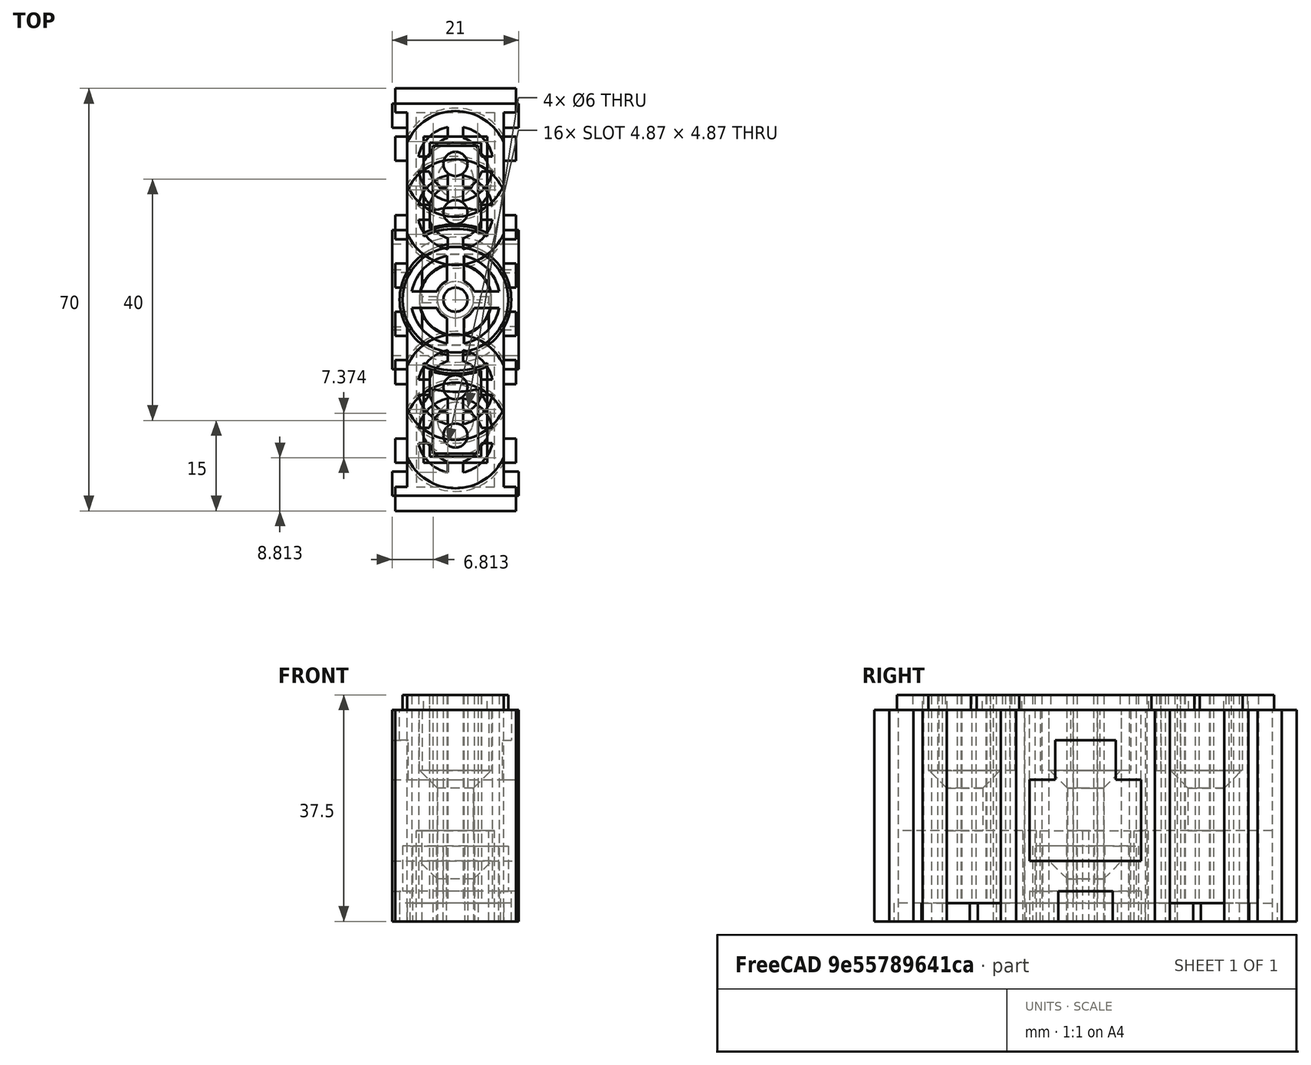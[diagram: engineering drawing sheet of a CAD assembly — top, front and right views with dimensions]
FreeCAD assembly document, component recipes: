
FREECAD ASSEMBLY — COMPONENT RECIPES ("PipeMountDistance")

This assembly document has 5 components, labeled P0..P4 below (a component is one placed body or linked part). 5 of them carry a construction recipe — the FreeCAD feature program that regenerates the part from scratch, quoted from this document or its linked companion documents; the rest are supplied as boundary geometry only. No exploded tour is included for this assembly.
COMPONENT P0 — recipe-attached ("Dual Pipes 40mm", modeled in this document).
Construction recipe (the document's own serialized feature program — sketch geometry with constraints, then the solid features built on it; lengths are millimeters unless a unit is written):

FEATURE [Sketcher::SketchObject] Sketch
  ArcFitTolerance = 1e-06
  AttachmentSupport = -> [XY_Plane]
  ExternalTypes = [0]
  FullyConstrained = true
  MakeInternals = false
  MapMode = 5
  sketch-geometry (23):
    g0: LineSegment StartX=-10.5 StartY=-11.5 StartZ=0 EndX=-10.5 EndY=11.5 EndZ=0
    g1: LineSegment StartX=-10.5 StartY=11.5 StartZ=0 EndX=-8 EndY=11.5 EndZ=0
    g2: LineSegment StartX=-8 StartY=11.5 StartZ=0 EndX=-8 EndY=28.5 EndZ=0
    g3: LineSegment StartX=-8 StartY=28.5 StartZ=0 EndX=-10.5 EndY=28.5 EndZ=0
    g4: LineSegment StartX=-10.5 StartY=28.5 StartZ=0 EndX=-10.5 EndY=32.5 EndZ=0
    g5: LineSegment StartX=-10.5 StartY=32.5 StartZ=0 EndX=10.5 EndY=32.5 EndZ=0
    g6: LineSegment StartX=10.5 StartY=32.5 StartZ=0 EndX=10.5 EndY=28.5 EndZ=0
    g7: LineSegment StartX=10.5 StartY=28.5 StartZ=0 EndX=8 EndY=28.5 EndZ=0
    g8: LineSegment StartX=8 StartY=28.5 StartZ=0 EndX=8 EndY=11.5 EndZ=0
    g9: LineSegment StartX=8 StartY=11.5 StartZ=0 EndX=10.5 EndY=11.5 EndZ=0
    g10: LineSegment StartX=10.5 StartY=11.5 StartZ=0 EndX=10.5 EndY=-11.5 EndZ=0
    g11: LineSegment StartX=10.5 StartY=-11.5 StartZ=0 EndX=8 EndY=-11.5 EndZ=0
    g12: LineSegment StartX=8 StartY=-11.5 StartZ=0 EndX=8 EndY=-28.5 EndZ=0
    g13: LineSegment StartX=8 StartY=-28.5 StartZ=0 EndX=10.5 EndY=-28.5 EndZ=0
    g14: LineSegment StartX=10.5 StartY=-28.5 StartZ=0 EndX=10.5 EndY=-32.5 EndZ=0
    g15: LineSegment StartX=10.5 StartY=-32.5 StartZ=0 EndX=-10.5 EndY=-32.5 EndZ=0
    g16: LineSegment StartX=-10.5 StartY=-32.5 StartZ=0 EndX=-10.5 EndY=-28.5 EndZ=0
    g17: LineSegment StartX=-10.5 StartY=-28.5 StartZ=0 EndX=-8 EndY=-28.5 EndZ=0
    g18: LineSegment StartX=-8 StartY=-28.5 StartZ=0 EndX=-8 EndY=-11.5 EndZ=0
    g19: LineSegment StartX=-8 StartY=-11.5 StartZ=0 EndX=-10.5 EndY=-11.5 EndZ=0
    g20: Circle CenterX=0 CenterY=0 CenterZ=0 NormalX=0 NormalY=0 NormalZ=1 AngleXU=0 Radius=2
    g21: Circle CenterX=0 CenterY=20 CenterZ=0 NormalX=0 NormalY=0 NormalZ=1 AngleXU=0 Radius=3
    g22: Circle CenterX=0 CenterY=-20 CenterZ=0 NormalX=0 NormalY=0 NormalZ=1 AngleXU=0 Radius=3
  constraints (65):
    c: Vertical(g0)
    c: Coincident(g0,g1)
    c: Coincident(g1,g2)
    c: Coincident(g2,g3)
    c: Coincident(g3,g4)
    c: Coincident(g4,g5)
    c: Coincident(g5,g6)
    c: Coincident(g6,g7)
    c: Coincident(g7,g8)
    c: Coincident(g8,g9)
    c: Horizontal(g9)
    c: Coincident(g9,g10)
    c: Coincident(g10,g11)
    c: Coincident(g11,g12)
    c: Vertical(g12)
    c: Coincident(g12,g13)
    c: Horizontal(g13)
    c: Coincident(g13,g14)
    c: Coincident(g14,g15)
    c: Horizontal(g15)
    c: Coincident(g15,g16)
    c: Coincident(g16,g17)
    c: Horizontal(g17)
    c: Coincident(g17,g18)
    c: Coincident(g18,g19)
    c: Coincident(g19,g0)
    c: Horizontal(g3)
    c: Horizontal(g1)
    c: Horizontal(g19)
    c: Horizontal(g11)
    c: Horizontal(g7)
    c: Vertical(g6)
    c: Vertical(g2)
    c: Vertical(g8)
    c: Vertical(g18)
    c: Vertical(g16)
    c: Vertical(g14)
    c: Symmetric(g4,g5,g-2)
    c: Symmetric(g9,g10,g-1)
    c: Equal(g5,g15)
    c: Equal(g7,g9)
    c: DistanceX(g2,g7) = 16  'MinorWidth'
    c: DistanceX(g5,g5) = 21  'MajorWidth'
    c: DistanceY(g15,g4) = 65  'MinorHeight'
    c: DistanceY(g2,g2) = 17  'CutoutHeight'
    c: Diameter(g20) = 4  'ScrewHoleDia'
    c: PointOnObject(g21,g-2)
    c: Symmetric(g22,g21,g-1)
    c: DistanceY(g22,g21) = 40
    c: Equal(g21,g22)
    c: Diameter(g22) = 6  'MountHoleDia'
    c: Coincident(g20,g-1)
    c: Vertical(g4)
    c: Equal(g6,g4)
    c: Equal(g4,g16)
    c: Equal(g16,g14)
    c: Symmetric(g4,g15,g-1)
    c: Equal(g3,g19)
    c: Equal(g19,g11)
    c: Equal(g11,g7)
    c: Equal(g10,g0)
    c: Equal(g2,g8)
    c: DistanceY(g0,g0) = 23
    c: Vertical(g1,g18)
    c: DistanceY(g6,g6) = 4
FEATURE [PartDesign::Pad] Pad
  Direction = (0,0,1)
  Length = 35
  Length2 = 10
  Profile = -> Sketch
  ReferenceAxis = -> Sketch [N_Axis]
  Refine = true
  Suppressed = false
  Type = 0
FEATURE [Sketcher::SketchObject] Sketch001
  ArcFitTolerance = 1e-06
  AttachmentSupport = -> [Pad]
  ExternalTypes = [0]
  FullyConstrained = true
  MakeInternals = false
  MapMode = 5
  Placement = pos=(0,0,0) rot=(1,0,0;3.14159rad)
  sketch-geometry (1):
    g0: Circle CenterX=0 CenterY=0 CenterZ=0 NormalX=0 NormalY=0 NormalZ=1 AngleXU=0 Radius=9.25
  constraints (2):
    c: Diameter(g0) = 18.5  'PadDia'
    c: Coincident(g0,g-1)
FEATURE [PartDesign::Pocket] Pocket
  BaseFeature = -> Pad
  Direction = (0,0,1)
  Length = 3
  Length2 = 5
  Profile = -> Sketch001
  ReferenceAxis = -> Sketch001 [N_Axis]
  Refine = true
  Suppressed = false
  Type = 0
FEATURE [Sketcher::SketchObject] Sketch002
  ArcFitTolerance = 1e-06
  AttachmentSupport = -> [Pocket]
  ExternalGeometry = -> [Pocket]
  ExternalTypes = [0]
  FullyConstrained = true
  MakeInternals = false
  MapMode = 5
  Placement = pos=(0,0,35) rot=(0,0,1;0rad)
  expr: .Constraints.MinorPadDia = <<Sketch001>>.Constraints.PadDia - 1 mm
  expr: .Constraints.WidePadDia = .Constraints.MinorPadDia + 6 mm
  sketch-geometry (12):
    g0: Circle CenterX=0 CenterY=0 CenterZ=0 NormalX=0 NormalY=0 NormalZ=1 AngleXU=0 Radius=8.75
    g1: Circle CenterX=0 CenterY=0 CenterZ=0 NormalX=0 NormalY=0 NormalZ=1 AngleXU=0 Radius=2
    g2: Circle CenterX=0 CenterY=20 CenterZ=0 NormalX=0 NormalY=0 NormalZ=1 AngleXU=0 Radius=3
    g3: Circle CenterX=0 CenterY=-20 CenterZ=0 NormalX=0 NormalY=0 NormalZ=1 AngleXU=0 Radius=3
    g4: LineSegment StartX=-5.25 StartY=10.5119 StartZ=0 EndX=-5.25 EndY=27 EndZ=0
    g5: LineSegment StartX=-5.25 StartY=27 StartZ=0 EndX=5.25 EndY=27 EndZ=0
    g6: LineSegment StartX=5.25 StartY=27 StartZ=0 EndX=5.25 EndY=10.5119 EndZ=0
    g7: LineSegment StartX=-5.25 StartY=-10.5119 StartZ=0 EndX=-5.25 EndY=-27 EndZ=0
    g8: LineSegment StartX=-5.25 StartY=-27 StartZ=0 EndX=5.25 EndY=-27 EndZ=0
    g9: LineSegment StartX=5.25 StartY=-27 StartZ=0 EndX=5.25 EndY=-10.5119 EndZ=0
    g10: ArcOfCircle CenterX=0 CenterY=0 CenterZ=0 NormalX=0 NormalY=0 NormalZ=1 AngleXU=0 Radius=11.75 StartAngle=1.1076 EndAngle=2.03399
    g11: ArcOfCircle CenterX=0 CenterY=0 CenterZ=0 NormalX=0 NormalY=0 NormalZ=1 AngleXU=0 Radius=11.75 StartAngle=4.24919 EndAngle=5.17558
  constraints (33):
    c: Coincident(g0,g-1)
    c: Coincident(g1,g0)
    c: Equal(g-3,g1)
    c: Diameter(g0) = 17.5  'MinorPadDia'
    c: Coincident(g2,g-4)
    c: Symmetric(g3,g2,g-1)
    c: Equal(g2,g3)
    c: Equal(g2,g-4)
    c: Vertical(g4)
    c: Coincident(g4,g5)
    c: Horizontal(g5)
    c: Coincident(g5,g6)
    c: Vertical(g6)
    c: Vertical(g7)
    c: Coincident(g7,g8)
    c: Horizontal(g8)
    c: Coincident(g8,g9)
    c: Vertical(g9)
    c: Equal(g5,g8)
    c: Equal(g9,g7)
    c: Equal(g7,g4)
    c: Equal(g4,g6)
    c: Coincident(g10,g4)
    c: Coincident(g10,g6)
    c: Coincident(g11,g7)
    c: Coincident(g11,g9)
    c: Coincident(g11,g10)
    c: Coincident(g11,g0)
    c: Equal(g10,g11)
    c: Diameter(g10) = 23.5  'WidePadDia'
    c: DistanceX(g5,g-6) = 2.75  'OuterWallWidth'
    c: DistanceX(g5,g5) = 10.5
    c: DistanceY(g7,g4) = 54
FEATURE [PartDesign::Pad] Pad001
  BaseFeature = -> Pocket
  Direction = (0,0,1)
  Length = 2.5
  Length2 = 10
  Profile = -> Sketch002
  ReferenceAxis = -> Sketch002 [N_Axis]
  Refine = true
  Suppressed = false
  Type = 0
FEATURE [Sketcher::SketchObject] Sketch003
  ArcFitTolerance = 1e-06
  AttachmentSupport = -> [Pad001]
  ExternalGeometry = -> [Pad001]
  ExternalTypes = [0]
  FullyConstrained = true
  MakeInternals = false
  MapMode = 5
  Placement = pos=(0,0,37.5) rot=(0,0,1;0rad)
  expr: Constraints[22] = .Constraints.InnerWallWidth
  expr: Constraints[23] = Sketch002.Constraints.WidePadDia + .Constraints.InnerWallWidth * 1.5
  sketch-geometry (8):
    g0: LineSegment StartX=-4.25 StartY=11.7553 StartZ=0 EndX=-4.25 EndY=26 EndZ=0
    g1: LineSegment StartX=-4.25 StartY=26 StartZ=0 EndX=4.25 EndY=26 EndZ=0
    g2: LineSegment StartX=4.25 StartY=26 StartZ=0 EndX=4.25 EndY=11.7553 EndZ=0
    g3: LineSegment StartX=-4.25 StartY=-11.7553 StartZ=0 EndX=-4.25 EndY=-26 EndZ=0
    g4: LineSegment StartX=-4.25 StartY=-26 StartZ=0 EndX=4.25 EndY=-26 EndZ=0
    g5: LineSegment StartX=4.25 StartY=-26 StartZ=0 EndX=4.25 EndY=-11.7553 EndZ=0
    g6: ArcOfCircle CenterX=0 CenterY=0 CenterZ=0 NormalX=0 NormalY=0 NormalZ=1 AngleXU=0 Radius=12.5 StartAngle=4.36547 EndAngle=5.05931
    g7: ArcOfCircle CenterX=0 CenterY=0 CenterZ=0 NormalX=0 NormalY=0 NormalZ=1 AngleXU=0 Radius=12.5 StartAngle=1.22388 EndAngle=1.91771
  constraints (26):
    c: Vertical(g0)
    c: Coincident(g0,g1)
    c: Horizontal(g1)
    c: Coincident(g1,g2)
    c: Vertical(g2)
    c: Vertical(g3)
    c: Coincident(g3,g4)
    c: Horizontal(g4)
    c: Coincident(g4,g5)
    c: Vertical(g5)
    c: Coincident(g6,g3)
    c: Coincident(g6,g5)
    c: Coincident(g7,g0)
    c: Coincident(g7,g2)
    c: Coincident(g6,g-1)
    c: Coincident(g6,g7)
    c: Equal(g2,g0)
    c: Equal(g0,g3)
    c: Equal(g3,g5)
    c: Equal(g6,g7)
    c: Equal(g4,g1)
    c: DistanceX(g1,g-4) = 1  'InnerWallWidth'
    c: DistanceY(g1,g-4) = 1
    c: Diameter(g7) = 25
    c: Diameter(g-5) = 17.5  'D2'
    c: Diameter(g-6) = 23.5  'D3'
FEATURE [PartDesign::Pocket] Pocket001
  BaseFeature = -> Pad001
  Direction = (0,0,-1)
  Length = 0
  Length2 = 5
  Offset = 25
  Profile = -> Sketch003
  ReferenceAxis = -> Sketch003 [N_Axis]
  Refine = true
  Suppressed = false
  Type = 3
  UpToFace = -> Pad001 [Face4]
FEATURE [Sketcher::SketchObject] Sketch004
  ArcFitTolerance = 1e-06
  AttachmentSupport = -> [Pocket001]
  ExternalGeometry = -> [Pocket001]
  ExternalTypes = [0]
  FullyConstrained = true
  MakeInternals = false
  MapMode = 5
  Placement = pos=(0,0,37.5) rot=(0,0,1;0rad)
  expr: Constraints[44] = <<Sketch002>>.Constraints.OuterWallWidth
  expr: Constraints[45] = <<Sketch002>>.Constraints.OuterWallWidth
  expr: Constraints[48] = <<Sketch002>>.Constraints.MinorPadDia - <<Sketch002>>.Constraints.OuterWallWidth
  expr: Constraints[49] = <<Sketch>>.Constraints.ScrewHoleDia + <<Sketch002>>.Constraints.OuterWallWidth
  sketch-geometry (16):
    g0: ArcOfCircle CenterX=0 CenterY=0 CenterZ=0 NormalX=0 NormalY=0 NormalZ=1 AngleXU=0 Radius=7.375 StartAngle=1.75833 EndAngle=2.95405
    g1: ArcOfCircle CenterX=0 CenterY=0 CenterZ=0 NormalX=0 NormalY=0 NormalZ=1 AngleXU=0 Radius=3.375 StartAngle=1.99041 EndAngle=2.72198
    g2: ArcOfCircle CenterX=-3e-16 CenterY=9e-16 CenterZ=0 NormalX=0 NormalY=0 NormalZ=1 AngleXU=0 Radius=7.375 StartAngle=0.187538 EndAngle=1.38326
    g3: ArcOfCircle CenterX=0 CenterY=0 CenterZ=0 NormalX=0 NormalY=0 NormalZ=1 AngleXU=0 Radius=3.375 StartAngle=0.419613 EndAngle=1.15118
    g4: ArcOfCircle CenterX=0 CenterY=0 CenterZ=0 NormalX=0 NormalY=0 NormalZ=1 AngleXU=0 Radius=3.375 StartAngle=5.132 EndAngle=5.86357
    g5: ArcOfCircle CenterX=0 CenterY=0 CenterZ=0 NormalX=0 NormalY=0 NormalZ=1 AngleXU=0 Radius=7.375 StartAngle=4.89993 EndAngle=6.09565
    g6: ArcOfCircle CenterX=0 CenterY=0 CenterZ=0 NormalX=0 NormalY=0 NormalZ=1 AngleXU=0 Radius=3.375 StartAngle=3.56121 EndAngle=4.29278
    g7: ArcOfCircle CenterX=-8e-16 CenterY=2e-16 CenterZ=0 NormalX=0 NormalY=0 NormalZ=1 AngleXU=0 Radius=7.375 StartAngle=3.32913 EndAngle=4.52485
    g8: LineSegment StartX=3.08221 StartY=1.375 StartZ=0 EndX=7.24569 EndY=1.375 EndZ=0
    g9: LineSegment StartX=3.08221 StartY=-1.375 StartZ=0 EndX=7.24569 EndY=-1.375 EndZ=0
    g10: LineSegment StartX=-1.375 StartY=3.08221 StartZ=0 EndX=-1.375 EndY=7.24569 EndZ=0
    g11: LineSegment StartX=1.375 StartY=3.08221 StartZ=0 EndX=1.375 EndY=7.24569 EndZ=0
    g12: LineSegment StartX=-3.08221 StartY=1.375 StartZ=0 EndX=-7.24569 EndY=1.375 EndZ=0
    g13: LineSegment StartX=-7.24569 StartY=-1.375 StartZ=0 EndX=-3.08221 EndY=-1.375 EndZ=0
    g14: LineSegment StartX=1.375 StartY=-7.24569 StartZ=0 EndX=1.375 EndY=-3.08221 EndZ=0
    g15: LineSegment StartX=-1.375 StartY=-7.24569 StartZ=0 EndX=-1.375 EndY=-3.08221 EndZ=0
  constraints (52):
    c: Coincident(g4,g5)
    c: Coincident(g4,g6)
    c: Coincident(g4,g0)
    c: Coincident(g4,g1)
    c: Coincident(g4,g3)
    c: Coincident(g4,g-1)
    c: Equal(g3,g4)
    c: Equal(g4,g6)
    c: Equal(g6,g1)
    c: Equal(g0,g2)
    c: Equal(g2,g5)
    c: Equal(g5,g7)
    c: Coincident(g8,g3)
    c: Coincident(g8,g2)
    c: Horizontal(g8)
    c: Coincident(g9,g4)
    c: Coincident(g9,g5)
    c: Horizontal(g9)
    c: Coincident(g10,g1)
    c: Coincident(g10,g0)
    c: Coincident(g11,g3)
    c: Coincident(g11,g2)
    c: Coincident(g12,g1)
    c: Coincident(g12,g0)
    c: Coincident(g13,g7)
    c: Coincident(g13,g6)
    c: Horizontal(g13)
    c: Coincident(g14,g5)
    c: Coincident(g14,g4)
    c: Coincident(g15,g7)
    c: Coincident(g15,g6)
    c: Vertical(g15)
    c: Vertical(g14)
    c: Vertical(g11)
    c: Vertical(g10)
    c: Horizontal(g12)
    c: Vertical(g5,g2)
    c: Vertical(g4,g3)
    c: Vertical(g6,g1)
    c: Vertical(g7,g0)
    c: Horizontal(g0,g2)
    c: Horizontal(g1,g3)
    c: Horizontal(g6,g4)
    c: Horizontal(g7,g5)
    c: DistanceY(g5,g2) = 2.75
    c: DistanceX(g0,g2) = 2.75
    c: Diameter(g-3) = 17.5
    c: Diameter(g-4) = 4
    c: Diameter(g2) = 14.75
    c: Diameter(g3) = 6.75
    c: Horizontal(g1,g3)
    c: Vertical(g6,g1)
FEATURE [PartDesign::Pocket] Pocket002
  BaseFeature = -> Pocket001
  Direction = (0,0,-1)
  Length = 5
  Length2 = 5
  Profile = -> Sketch004
  ReferenceAxis = -> Sketch004 [N_Axis]
  Refine = true
  Suppressed = false
  Type = 1
FEATURE [Sketcher::SketchObject] Sketch005
  ArcFitTolerance = 1e-06
  AttachmentSupport = -> [Pocket002]
  ExternalGeometry = -> [Pocket002]
  ExternalTypes = [0]
  FullyConstrained = true
  MakeInternals = false
  MapMode = 5
  Placement = pos=(0,0,37.5) rot=(0,0,1;0rad)
  sketch-geometry (2):
    g0: Circle CenterX=0 CenterY=20 CenterZ=0 NormalX=0 NormalY=0 NormalZ=1 AngleXU=0 Radius=6
    g1: Circle CenterX=0 CenterY=-20 CenterZ=0 NormalX=0 NormalY=0 NormalZ=1 AngleXU=0 Radius=6
  constraints (4):
    c: Coincident(g0,g-3)
    c: Equal(g1,g0)
    c: Symmetric(g1,g0,g-1)
    c: Diameter(g0) = 12
FEATURE [PartDesign::Pocket] Pocket003
  BaseFeature = -> Pocket002
  Direction = (0,0,-1)
  Length = 0
  Length2 = 5
  Profile = -> Sketch005
  ReferenceAxis = -> Sketch005 [N_Axis]
  Refine = true
  Suppressed = false
  Type = 3
  UpToFace = -> Pocket002 [Face35]
FEATURE [Sketcher::SketchObject] Sketch006
  ArcFitTolerance = 1e-06
  ExternalTypes = [0]
  FullyConstrained = true
  MakeInternals = false
  MapMode = 5
  Placement = pos=(0,0,0) rot=(1,0,0;3.14159rad)
  expr: Constraints[16] = .Constraints.BottomWallWidth
  expr: Constraints[23] = Sketch001.Constraints.PadDia + .Constraints.BottomWallWidth * 1.5
  sketch-geometry (8):
    g0: LineSegment StartX=-6.5 StartY=8.08645 StartZ=0 EndX=-6.5 EndY=31 EndZ=0
    g1: LineSegment StartX=-6.5 StartY=31 StartZ=0 EndX=6.5 EndY=31 EndZ=0
    g2: LineSegment StartX=6.5 StartY=31 StartZ=0 EndX=6.5 EndY=8.08645 EndZ=0
    g3: LineSegment StartX=-6.5 StartY=-8.08645 StartZ=0 EndX=-6.5 EndY=-31 EndZ=0
    g4: LineSegment StartX=-6.5 StartY=-31 StartZ=0 EndX=6.5 EndY=-31 EndZ=0
    g5: LineSegment StartX=6.5 StartY=-31 StartZ=0 EndX=6.5 EndY=-8.08645 EndZ=0
    g6: ArcOfCircle CenterX=0 CenterY=0 CenterZ=0 NormalX=0 NormalY=0 NormalZ=1 AngleXU=0 Radius=10.375 StartAngle=4.03533 EndAngle=5.38945
    g7: ArcOfCircle CenterX=0 CenterY=0 CenterZ=0 NormalX=0 NormalY=0 NormalZ=1 AngleXU=0 Radius=10.375 StartAngle=0.893734 EndAngle=2.24786
  constraints (25):
    c: Vertical(g0)
    c: Coincident(g0,g1)
    c: Horizontal(g1)
    c: Coincident(g1,g2)
    c: Vertical(g2)
    c: Vertical(g3)
    c: Coincident(g3,g4)
    c: Horizontal(g4)
    c: Coincident(g4,g5)
    c: Vertical(g5)
    c: Coincident(g6,g3)
    c: Coincident(g6,g5)
    c: Coincident(g7,g0)
    c: Coincident(g7,g2)
    c: Coincident(g7,g6)
    c: Coincident(g7,g-1)
    c: DistanceY(g1,g-3) = 1.5
    c: DistanceX(g1,g-4) = 1.5  'BottomWallWidth'
    c: Equal(g2,g0)
    c: Equal(g0,g3)
    c: Equal(g3,g5)
    c: Equal(g6,g7)
    c: Diameter(g-5) = 18
    c: Diameter(g7) = 20.75
    c: Equal(g4,g1)
FEATURE [PartDesign::Pocket] Pocket004
  BaseFeature = -> Pocket003
  Direction = (0,0,1)
  Length = 0
  Length2 = 5
  Offset = 10
  Profile = -> Sketch006
  ReferenceAxis = -> Sketch006 [N_Axis]
  Refine = true
  Suppressed = false
  Type = 3
  UpToFace = -> Pocket003 [Face75]
FEATURE [PartDesign::Chamfer] Chamfer
  Angle = 45
  Base = -> Pocket004 [Edge191,Edge222]
  BaseFeature = -> Pocket004
  ChamferType = 0
  FlipDirection = false
  Refine = true
  Size = 2.9
  Size2 = 1
  SupportTransform = false
  Suppressed = false
  UseAllEdges = false
FEATURE [PartDesign::Body] Body  label="Dual Pipes 40mm"
  AllowCompound = false
  Group = -> [Sketch,Pad,Sketch001,Pocket,Sketch002,Pad001,Sketch003,Pocket001,Sketch004,Pocket002,Sketch005,Pocket003,Sketch006,Pocket004,Chamfer]
  Origin = -> Origin
  Tip = -> Chamfer
COMPONENT P1 — recipe-attached ("Dual Pipes 45mm", modeled in this document).
Construction recipe (the document's own serialized feature program — sketch geometry with constraints, then the solid features built on it; lengths are millimeters unless a unit is written):

FEATURE [Sketcher::SketchObject] Sketch007
  ArcFitTolerance = 1e-06
  AttachmentSupport = -> [XY_Plane001]
  ExternalTypes = [0]
  FullyConstrained = true
  MakeInternals = false
  MapMode = 5
  sketch-geometry (32):
    g0: LineSegment StartX=-10 StartY=35 StartZ=0 EndX=-10 EndY=31 EndZ=0
    g1: LineSegment StartX=-10 StartY=31 StartZ=0 EndX=-8 EndY=31 EndZ=0
    g2: LineSegment StartX=-8 StartY=31 StartZ=0 EndX=-8 EndY=14 EndZ=0
    g3: LineSegment StartX=-8 StartY=14 StartZ=0 EndX=-10 EndY=14 EndZ=0
    g4: LineSegment StartX=-10 StartY=-14 StartZ=0 EndX=-8 EndY=-14 EndZ=0
    g5: LineSegment StartX=-8 StartY=-14 StartZ=0 EndX=-8 EndY=-31 EndZ=0
    g6: LineSegment StartX=-8 StartY=-31 StartZ=0 EndX=-10 EndY=-31 EndZ=0
    g7: LineSegment StartX=-10 StartY=-31 StartZ=0 EndX=-10 EndY=-35 EndZ=0
    g8: LineSegment StartX=-10 StartY=-35 StartZ=0 EndX=10 EndY=-35 EndZ=0
    g9: LineSegment StartX=10 StartY=-35 StartZ=0 EndX=10 EndY=-31 EndZ=0
    g10: LineSegment StartX=10 StartY=-31 StartZ=0 EndX=8 EndY=-31 EndZ=0
    g11: LineSegment StartX=8 StartY=-31 StartZ=0 EndX=8 EndY=-14 EndZ=0
    g12: LineSegment StartX=8 StartY=-14 StartZ=0 EndX=10 EndY=-14 EndZ=0
    g13: LineSegment StartX=10 StartY=14 StartZ=0 EndX=8 EndY=14 EndZ=0
    g14: LineSegment StartX=8 StartY=14 StartZ=0 EndX=8 EndY=31 EndZ=0
    g15: LineSegment StartX=8 StartY=31 StartZ=0 EndX=10 EndY=31 EndZ=0
    g16: LineSegment StartX=10 StartY=31 StartZ=0 EndX=10 EndY=35 EndZ=0
    g17: LineSegment StartX=10 StartY=35 StartZ=0 EndX=-10 EndY=35 EndZ=0
    g18: Circle CenterX=0 CenterY=22.5 CenterZ=0 NormalX=0 NormalY=0 NormalZ=1 AngleXU=0 Radius=2
    g19: Circle CenterX=0 CenterY=-22.5 CenterZ=0 NormalX=0 NormalY=0 NormalZ=1 AngleXU=0 Radius=2
    g20: LineSegment [constr] StartX=0 StartY=22.5 StartZ=0 EndX=-8 EndY=22.5 EndZ=0
    g21: LineSegment StartX=-10 StartY=14 StartZ=0 EndX=-10 EndY=10 EndZ=0
    g22: LineSegment StartX=-10 StartY=10 StartZ=0 EndX=-8 EndY=10 EndZ=0
    g23: LineSegment StartX=-8 StartY=10 StartZ=0 EndX=-8 EndY=-10 EndZ=0
    g24: LineSegment StartX=-8 StartY=-10 StartZ=0 EndX=-10 EndY=-10 EndZ=0
    g25: LineSegment StartX=-10 StartY=-10 StartZ=0 EndX=-10 EndY=-14 EndZ=0
    g26: LineSegment StartX=10 StartY=-14 StartZ=0 EndX=10 EndY=-10 EndZ=0
    g27: LineSegment StartX=10 StartY=-10 StartZ=0 EndX=8 EndY=-10 EndZ=0
    g28: LineSegment StartX=8 StartY=-10 StartZ=0 EndX=8 EndY=10 EndZ=0
    g29: LineSegment StartX=8 StartY=10 StartZ=0 EndX=10 EndY=10 EndZ=0
    g30: LineSegment StartX=10 StartY=10 StartZ=0 EndX=10 EndY=14 EndZ=0
    g31: Circle CenterX=0 CenterY=0 CenterZ=0 NormalX=0 NormalY=0 NormalZ=1 AngleXU=0 Radius=3
  constraints (90):
    c: Vertical(g0)
    c: Coincident(g0,g1)
    c: Coincident(g1,g2)
    c: Vertical(g2)
    c: Coincident(g2,g3)
    c: Horizontal(g3)
    c: Horizontal(g4)
    c: Coincident(g4,g5)
    c: Coincident(g5,g6)
    c: Horizontal(g6)
    c: Coincident(g6,g7)
    c: Vertical(g7)
    c: Coincident(g7,g8)
    c: Horizontal(g8)
    c: Coincident(g8,g9)
    c: Coincident(g9,g10)
    c: Coincident(g10,g11)
    c: Coincident(g11,g12)
    c: Coincident(g13,g14)
    c: Vertical(g14)
    c: Coincident(g14,g15)
    c: Horizontal(g15)
    c: Coincident(g15,g16)
    c: Coincident(g16,g17)
    c: Coincident(g17,g0)
    c: Horizontal(g1)
    c: Horizontal(g13)
    c: Horizontal(g12)
    c: Horizontal(g10)
    c: Vertical(g5)
    c: Vertical(g16)
    c: Vertical(g11)
    c: Vertical(g9)
    c: Symmetric(g8,g16,g-1)
    c: Symmetric(g3,g4,g-1)
    c: Symmetric(g0,g16,g-2)
    c: Vertical(g0,g3)
    c: Vertical(g3,g6)
    c: Vertical(g13,g9)
    c: Equal(g9,g7)
    c: Equal(g7,g0)
    c: Equal(g0,g16)
    c: Equal(g15,g3)
    c: Equal(g13,g12)
    c: Equal(g12,g4)
    c: DistanceX(g17,g17) = 20
    c: DistanceX(g1,g14) = 16
    c: PointOnObject(g18,g-2)
    c: Equal(g19,g18)
    c: Symmetric(g19,g18,g-1)
    c: Diameter(g18) = 4  'ScrewHoleDia'
    c: DistanceY(g2,g2) = 17
    c: Coincident(g20,g18)
    c: Symmetric(g2,g2,g20)
    c: Horizontal(g20)
    c: DistanceY(g16,g16) = 4
    c: DistanceY(g19,g18) = 45
    c: Equal(g14,g2)
    c: Equal(g5,g11)
    c: Coincident(g3,g21)
    c: Vertical(g21)
    c: Coincident(g21,g22)
    c: Coincident(g22,g23)
    c: Vertical(g23)
    c: Coincident(g23,g24)
    c: Horizontal(g24)
    c: Coincident(g24,g25)
    c: Coincident(g25,g4)
    c: Coincident(g12,g26)
    c: Coincident(g26,g27)
    c: Coincident(g27,g28)
    c: Vertical(g28)
    c: Coincident(g28,g29)
    c: Coincident(g29,g30)
    c: Coincident(g30,g13)
    c: Vertical(g30)
    c: Vertical(g25)
    c: Vertical(g26)
    c: Horizontal(g27)
    c: Horizontal(g22)
    c: Horizontal(g29)
    c: Equal(g0,g21)
    c: Equal(g21,g30)
    c: Equal(g30,g26)
    c: Equal(g26,g25)
    c: Vertical(g28,g13)
    c: Vertical(g22,g2)
    c: Vertical(g26,g29)
    c: Coincident(g31,g-1)
    c: Diameter(g31) = 6
FEATURE [PartDesign::Pad] Pad002
  Direction = (0,0,1)
  Length = 35
  Length2 = 10
  Profile = -> Sketch007
  ReferenceAxis = -> Sketch007 [N_Axis]
  Refine = true
  Suppressed = false
  Type = 0
FEATURE [Sketcher::SketchObject] Sketch008
  ArcFitTolerance = 1e-06
  AttachmentSupport = -> [Pad002]
  ExternalGeometry = -> [Pad002]
  ExternalTypes = [0]
  FullyConstrained = true
  MakeInternals = false
  MapMode = 5
  Placement = pos=(0,0,0) rot=(1,0,0;3.14159rad)
  sketch-geometry (2):
    g0: Circle CenterX=0 CenterY=22.5 CenterZ=0 NormalX=0 NormalY=0 NormalZ=1 AngleXU=0 Radius=9.25
    g1: Circle CenterX=0 CenterY=-22.5 CenterZ=0 NormalX=0 NormalY=0 NormalZ=1 AngleXU=0 Radius=9.25
  constraints (4):
    c: Coincident(g0,g-3)
    c: Coincident(g1,g-4)
    c: Equal(g1,g0)
    c: Diameter(g0) = 18.5
FEATURE [PartDesign::Pocket] Pocket005
  BaseFeature = -> Pad002
  Direction = (0,0,1)
  Length = 3
  Length2 = 5
  Profile = -> Sketch008
  ReferenceAxis = -> Sketch008 [N_Axis]
  Refine = true
  Suppressed = false
  Type = 0
FEATURE [Sketcher::SketchObject] Sketch009
  ArcFitTolerance = 1e-06
  AttachmentSupport = -> [Pocket005]
  ExternalGeometry = -> [Pocket005]
  ExternalTypes = [0]
  FullyConstrained = true
  MakeInternals = false
  MapMode = 5
  Placement = pos=(0,0,35) rot=(0,0,1;0rad)
  sketch-geometry (10):
    g0: LineSegment StartX=-8 StartY=26.0444 StartZ=0 EndX=-8 EndY=18.9556 EndZ=0
    g1: LineSegment StartX=8 StartY=26.0444 StartZ=0 EndX=8 EndY=18.9556 EndZ=0
    g2: LineSegment StartX=-8 StartY=-18.9556 StartZ=0 EndX=-8 EndY=-26.0444 EndZ=0
    g3: LineSegment StartX=8 StartY=-18.9556 StartZ=0 EndX=8 EndY=-26.0444 EndZ=0
    g4: ArcOfCircle CenterX=0 CenterY=22.5 CenterZ=0 NormalX=0 NormalY=0 NormalZ=1 AngleXU=0 Radius=8.75 StartAngle=0.417055 EndAngle=2.72454
    g5: ArcOfCircle CenterX=0 CenterY=22.5 CenterZ=0 NormalX=0 NormalY=0 NormalZ=1 AngleXU=0 Radius=8.75 StartAngle=3.55865 EndAngle=5.86613
    g6: ArcOfCircle CenterX=0 CenterY=-22.5 CenterZ=0 NormalX=0 NormalY=0 NormalZ=1 AngleXU=0 Radius=8.75 StartAngle=0.417055 EndAngle=2.72454
    g7: ArcOfCircle CenterX=0 CenterY=-22.5 CenterZ=0 NormalX=0 NormalY=0 NormalZ=1 AngleXU=0 Radius=8.75 StartAngle=3.55865 EndAngle=5.86613
    g8: Circle CenterX=0 CenterY=22.5 CenterZ=0 NormalX=0 NormalY=0 NormalZ=1 AngleXU=0 Radius=2
    g9: Circle CenterX=0 CenterY=-22.5 CenterZ=0 NormalX=0 NormalY=0 NormalZ=1 AngleXU=0 Radius=2
  constraints (28):
    c: Equal(g0,g1)
    c: Equal(g1,g3)
    c: Coincident(g5,g4)
    c: Coincident(g8,g4)
    c: Coincident(g1,g4)
    c: Coincident(g0,g4)
    c: Coincident(g0,g5)
    c: Coincident(g1,g5)
    c: Vertical(g0)
    c: Vertical(g2)
    c: Vertical(g3)
    c: Coincident(g4,g-3)
    c: Vertical(g0,g-5)
    c: Coincident(g6,g3)
    c: Coincident(g7,g3)
    c: Coincident(g6,g2)
    c: Coincident(g2,g7)
    c: Coincident(g6,g-4)
    c: Coincident(g7,g6)
    c: Coincident(g9,g6)
    c: Equal(g7,g6)
    c: Equal(g6,g5)
    c: Equal(g5,g4)
    c: Equal(g2,g3)
    c: Equal(g9,g8)
    c: Equal(g8,g-3)
    c: Diameter(g4) = 17.5  'PadMinorDia'
    c: Vertical(g1)
FEATURE [PartDesign::Pad] Pad003
  BaseFeature = -> Pocket005
  Direction = (0,0,1)
  Length = 2.5
  Length2 = 10
  Profile = -> Sketch009
  ReferenceAxis = -> Sketch009 [N_Axis]
  Refine = true
  Suppressed = false
  Type = 0
FEATURE [Sketcher::SketchObject] Sketch010
  ArcFitTolerance = 1e-06
  AttachmentSupport = -> [Pad003]
  ExternalGeometry = -> [Pad003]
  ExternalTypes = [0]
  FullyConstrained = true
  MakeInternals = false
  MapMode = 5
  Placement = pos=(0,0,37.5) rot=(0,0,1;0rad)
  expr: Constraints[45] = <<Sketch007>>.Constraints.ScrewHoleDia + .Constraints.WallThickness * 2
  expr: Constraints[46] = <<Sketch009>>.Constraints.PadMinorDia - .Constraints.WallThickness * 2
  sketch-geometry (32):
    g0: ArcOfCircle CenterX=0 CenterY=22.5 CenterZ=0 NormalX=0 NormalY=0 NormalZ=1 AngleXU=0 Radius=6.25 StartAngle=1.77215 EndAngle=2.94023
    g1: ArcOfCircle CenterX=0 CenterY=22.5 CenterZ=0 NormalX=0 NormalY=0 NormalZ=1 AngleXU=0 Radius=4.5 StartAngle=1.85228 EndAngle=2.86011
    g2: ArcOfCircle CenterX=0 CenterY=22.5 CenterZ=0 NormalX=0 NormalY=0 NormalZ=1 AngleXU=0 Radius=6.25 StartAngle=0.201358 EndAngle=1.36944
    g3: ArcOfCircle CenterX=0 CenterY=22.5 CenterZ=0 NormalX=0 NormalY=0 NormalZ=1 AngleXU=0 Radius=4.5 StartAngle=0.28148 EndAngle=1.28932
    g4: ArcOfCircle CenterX=0 CenterY=22.5 CenterZ=0 NormalX=0 NormalY=0 NormalZ=1 AngleXU=0 Radius=4.5 StartAngle=4.99387 EndAngle=6.00171
    g5: ArcOfCircle CenterX=0 CenterY=22.5 CenterZ=0 NormalX=0 NormalY=0 NormalZ=1 AngleXU=0 Radius=6.25 StartAngle=4.91375 EndAngle=6.08183
    g6: ArcOfCircle CenterX=0 CenterY=22.5 CenterZ=0 NormalX=0 NormalY=0 NormalZ=1 AngleXU=0 Radius=4.5 StartAngle=3.42307 EndAngle=4.43091
    g7: ArcOfCircle CenterX=0 CenterY=22.5 CenterZ=0 NormalX=0 NormalY=0 NormalZ=1 AngleXU=0 Radius=6.25 StartAngle=3.34295 EndAngle=4.51103
    g8: LineSegment StartX=-4.3229 StartY=21.25 StartZ=0 EndX=-6.12372 EndY=21.25 EndZ=0
    g9: LineSegment StartX=-6.12372 StartY=23.75 StartZ=0 EndX=-4.3229 EndY=23.75 EndZ=0
    g10: LineSegment StartX=-1.25 StartY=26.8229 StartZ=0 EndX=-1.25 EndY=28.6237 EndZ=0
    g11: LineSegment StartX=1.25 StartY=26.8229 StartZ=0 EndX=1.25 EndY=28.6237 EndZ=0
    g12: LineSegment StartX=4.3229 StartY=23.75 StartZ=0 EndX=6.12372 EndY=23.75 EndZ=0
    g13: LineSegment StartX=4.3229 StartY=21.25 StartZ=0 EndX=6.12372 EndY=21.25 EndZ=0
    g14: LineSegment StartX=1.25 StartY=18.1771 StartZ=0 EndX=1.25 EndY=16.3763 EndZ=0
    g15: LineSegment StartX=-1.25 StartY=16.3763 StartZ=0 EndX=-1.25 EndY=18.1771 EndZ=0
    g16: ArcOfCircle CenterX=0 CenterY=-22.5 CenterZ=0 NormalX=0 NormalY=0 NormalZ=1 AngleXU=0 Radius=6.25 StartAngle=3.34295 EndAngle=4.51103
    g17: ArcOfCircle CenterX=0 CenterY=-22.5 CenterZ=0 NormalX=0 NormalY=0 NormalZ=1 AngleXU=0 Radius=4.5 StartAngle=3.42307 EndAngle=4.43091
    g18: ArcOfCircle CenterX=0 CenterY=-22.5 CenterZ=0 NormalX=0 NormalY=0 NormalZ=1 AngleXU=0 Radius=6.25 StartAngle=4.91375 EndAngle=6.08183
    g19: ArcOfCircle CenterX=0 CenterY=-22.5 CenterZ=0 NormalX=0 NormalY=0 NormalZ=1 AngleXU=0 Radius=4.5 StartAngle=4.99387 EndAngle=6.00171
    g20: ArcOfCircle CenterX=0 CenterY=-22.5 CenterZ=0 NormalX=0 NormalY=0 NormalZ=1 AngleXU=0 Radius=4.5 StartAngle=0.28148 EndAngle=1.28932
    g21: ArcOfCircle CenterX=0 CenterY=-22.5 CenterZ=0 NormalX=0 NormalY=0 NormalZ=1 AngleXU=0 Radius=6.25 StartAngle=0.201358 EndAngle=1.36944
    g22: ArcOfCircle CenterX=0 CenterY=-22.5 CenterZ=0 NormalX=0 NormalY=0 NormalZ=1 AngleXU=0 Radius=4.5 StartAngle=1.85228 EndAngle=2.86011
    g23: ArcOfCircle CenterX=0 CenterY=-22.5 CenterZ=0 NormalX=0 NormalY=0 NormalZ=1 AngleXU=0 Radius=6.25 StartAngle=1.77215 EndAngle=2.94023
    g24: LineSegment StartX=-4.3229 StartY=-21.25 StartZ=0 EndX=-6.12372 EndY=-21.25 EndZ=0
    g25: LineSegment StartX=-6.12372 StartY=-23.75 StartZ=0 EndX=-4.3229 EndY=-23.75 EndZ=0
    g26: LineSegment StartX=-1.25 StartY=-26.8229 StartZ=0 EndX=-1.25 EndY=-28.6237 EndZ=0
    g27: LineSegment StartX=1.25 StartY=-26.8229 StartZ=0 EndX=1.25 EndY=-28.6237 EndZ=0
    g28: LineSegment StartX=4.3229 StartY=-23.75 StartZ=0 EndX=6.12372 EndY=-23.75 EndZ=0
    g29: LineSegment StartX=4.3229 StartY=-21.25 StartZ=0 EndX=6.12372 EndY=-21.25 EndZ=0
    g30: LineSegment StartX=1.25 StartY=-18.1771 StartZ=0 EndX=1.25 EndY=-16.3763 EndZ=0
    g31: LineSegment StartX=-1.25 StartY=-16.3763 StartZ=0 EndX=-1.25 EndY=-18.1771 EndZ=0
  constraints (95):
    c: Coincident(g8,g6)
    c: Coincident(g8,g7)
    c: Coincident(g9,g0)
    c: Coincident(g9,g1)
    c: Coincident(g10,g1)
    c: Coincident(g10,g0)
    c: Coincident(g11,g3)
    c: Coincident(g11,g2)
    c: Coincident(g12,g3)
    c: Coincident(g12,g2)
    c: Coincident(g13,g4)
    c: Coincident(g13,g5)
    c: Coincident(g14,g4)
    c: Coincident(g14,g5)
    c: Coincident(g15,g7)
    c: Coincident(g15,g6)
    c: Coincident(g4,g2)
    c: Coincident(g4,g3)
    c: Coincident(g4,g1)
    c: Coincident(g4,g0)
    c: Coincident(g4,g7)
    c: Coincident(g4,g6)
    c: Coincident(g4,g-3)
    c: Vertical(g10)
    c: Vertical(g11)
    c: Vertical(g15)
    c: Vertical(g14)
    c: Horizontal(g8)
    c: Horizontal(g13)
    c: Horizontal(g12)
    c: Horizontal(g9)
    c: Equal(g2,g5)
    c: Equal(g5,g7)
    c: Equal(g6,g4)
    c: Equal(g4,g3)
    c: Equal(g3,g1)
    c: Coincident(g5,g0)
    c: Symmetric(g0,g2,g-2)
    c: Vertical(g1,g6)
    c: Equal(g10,g9)
    c: Equal(g9,g8)
    c: Equal(g15,g14)
    c: Equal(g14,g13)
    c: Equal(g13,g12)
    c: DistanceX(g0,g2) = 2.5  'WallThickness'
    c: Diameter(g4) = 9
    c: Diameter(g5) = 12.5
    c: Coincident(g24,g22)
    c: Coincident(g24,g23)
    c: Coincident(g25,g16)
    c: Coincident(g25,g17)
    c: Coincident(g26,g17)
    c: Coincident(g26,g16)
    c: Coincident(g27,g19)
    c: Coincident(g27,g18)
    c: Coincident(g28,g19)
    c: Coincident(g28,g18)
    c: Coincident(g29,g20)
    c: Coincident(g29,g21)
    c: Coincident(g30,g20)
    c: Coincident(g30,g21)
    c: Coincident(g31,g23)
    c: Coincident(g31,g22)
    c: Coincident(g20,g18)
    c: Coincident(g20,g19)
    c: Coincident(g20,g17)
    c: Coincident(g20,g16)
    c: Coincident(g20,g23)
    c: Coincident(g20,g22)
    c: Vertical(g26)
    c: Vertical(g27)
    c: Vertical(g31)
    c: Vertical(g30)
    c: Horizontal(g24)
    c: Horizontal(g29)
    c: Horizontal(g28)
    c: Horizontal(g25)
    c: Equal(g18,g21)
    c: Equal(g21,g23)
    c: Equal(g22,g20)
    c: Equal(g20,g19)
    c: Equal(g19,g17)
    c: Coincident(g21,g16)
    c: Equal(g26,g25)
    c: Equal(g25,g24)
    c: Equal(g31,g30)
    c: Equal(g30,g29)
    c: Equal(g29,g28)
    c: Diameter(g20) = 9
    c: Diameter(g21) = 12.5
    c: Coincident(g16,g-4)
    c: Vertical(g5,g21)
    c: Vertical(g21,g19)
    c: Vertical(g22,g17)
    c: Horizontal(g22,g20)
FEATURE [PartDesign::Pocket] Pocket006
  BaseFeature = -> Pad003
  Direction = (0,0,-1)
  Length = 5
  Length2 = 5
  Profile = -> Sketch010
  ReferenceAxis = -> Sketch010 [N_Axis]
  Refine = true
  Suppressed = false
  Type = 1
FEATURE [Sketcher::SketchObject] Sketch011
  ArcFitTolerance = 1e-06
  AttachmentSupport = -> [Pocket006]
  ExternalGeometry = -> [Pocket006]
  ExternalTypes = [0]
  FullyConstrained = true
  MakeInternals = false
  MapMode = 5
  Placement = pos=(0,0,35) rot=(0,0,1;0rad)
  expr: Constraints[10] = <<Sketch010>>.Constraints.WallThickness
  expr: Constraints[11] = <<Sketch010>>.Constraints.WallThickness
  sketch-geometry (5):
    g0: LineSegment StartX=-5.5 StartY=7.5 StartZ=0 EndX=-5.5 EndY=-7.5 EndZ=0
    g1: LineSegment StartX=-5.5 StartY=-7.5 StartZ=0 EndX=5.5 EndY=-7.5 EndZ=0
    g2: LineSegment StartX=5.5 StartY=-7.5 StartZ=0 EndX=5.5 EndY=7.5 EndZ=0
    g3: LineSegment StartX=5.5 StartY=7.5 StartZ=0 EndX=-5.5 EndY=7.5 EndZ=0
    g4: GeomPoint [constr] X=0 Y=0 Z=0
  constraints (12):
    c: Coincident(g0,g1)
    c: Coincident(g1,g2)
    c: Coincident(g2,g3)
    c: Coincident(g3,g0)
    c: Vertical(g0)
    c: Vertical(g2)
    c: Horizontal(g1)
    c: Horizontal(g3)
    c: Symmetric(g2,g0,g4)
    c: Coincident(g4,g-1)
    c: DistanceY(g0,g-3) = 2.5
    c: DistanceX(g-3,g0) = 2.5
FEATURE [PartDesign::Pocket] Pocket007
  BaseFeature = -> Pocket006
  Direction = (0,0,-1)
  Length = 10
  Length2 = 5
  Profile = -> Sketch011
  ReferenceAxis = -> Sketch011 [N_Axis]
  Refine = true
  Suppressed = false
  Type = 0
FEATURE [Sketcher::SketchObject] Sketch012
  ArcFitTolerance = 1e-06
  AttachmentSupport = -> [Pocket007]
  ExternalGeometry = -> [Pocket007]
  ExternalTypes = [0]
  FullyConstrained = true
  MakeInternals = false
  MapMode = 5
  Placement = pos=(0,0,0) rot=(1,0,0;3.14159rad)
  expr: Constraints[10] = <<Sketch010>>.Constraints.WallThickness
  expr: Constraints[11] = <<Sketch010>>.Constraints.WallThickness
  sketch-geometry (5):
    g0: LineSegment StartX=-5.5 StartY=7.5 StartZ=0 EndX=-5.5 EndY=-7.5 EndZ=0
    g1: LineSegment StartX=-5.5 StartY=-7.5 StartZ=0 EndX=5.5 EndY=-7.5 EndZ=0
    g2: LineSegment StartX=5.5 StartY=-7.5 StartZ=0 EndX=5.5 EndY=7.5 EndZ=0
    g3: LineSegment StartX=5.5 StartY=7.5 StartZ=0 EndX=-5.5 EndY=7.5 EndZ=0
    g4: GeomPoint [constr] X=0 Y=0 Z=0
  constraints (12):
    c: Coincident(g0,g1)
    c: Coincident(g1,g2)
    c: Coincident(g2,g3)
    c: Coincident(g3,g0)
    c: Vertical(g0)
    c: Vertical(g2)
    c: Horizontal(g1)
    c: Horizontal(g3)
    c: Symmetric(g2,g0,g4)
    c: Coincident(g4,g-1)
    c: DistanceY(g0,g-3) = 2.5
    c: DistanceX(g-3,g0) = 2.5
FEATURE [PartDesign::Pocket] Pocket008
  BaseFeature = -> Pocket007
  Direction = (0,0,1)
  Length = 0
  Length2 = 5
  Offset = 10
  Profile = -> Sketch012
  ReferenceAxis = -> Sketch012 [N_Axis]
  Refine = true
  Suppressed = false
  Type = 3
  UpToFace = -> Pocket007 [Face66]
FEATURE [Sketcher::SketchObject] Sketch013
  ArcFitTolerance = 1e-06
  AttachmentSupport = -> [Pocket008]
  ExternalTypes = [0]
  FullyConstrained = true
  MakeInternals = false
  MapMode = 5
  Placement = pos=(0,0,35) rot=(0,0,1;0rad)
  sketch-geometry (1):
    g0: Circle CenterX=0 CenterY=0 CenterZ=0 NormalX=0 NormalY=0 NormalZ=1 AngleXU=0 Radius=6
  constraints (2):
    c: Coincident(g0,g-1)
    c: Diameter(g0) = 12
FEATURE [PartDesign::Pocket] Pocket009
  BaseFeature = -> Pocket008
  Direction = (0,0,-1)
  Length = 0
  Length2 = 5
  Profile = -> Sketch013
  ReferenceAxis = -> Sketch013 [N_Axis]
  Refine = true
  Suppressed = false
  Type = 3
  UpToFace = -> Pocket008 [Face70]
FEATURE [PartDesign::Chamfer] Chamfer001
  Angle = 45
  Base = -> Pocket009 [Edge273]
  BaseFeature = -> Pocket009
  ChamferType = 0
  FlipDirection = false
  Refine = true
  Size = 2.9
  Size2 = 1
  SupportTransform = false
  Suppressed = false
  UseAllEdges = false
FEATURE [PartDesign::Body] Body001  label="Dual Pipes 45mm"
  AllowCompound = false
  Group = -> [Sketch007,Pad002,Sketch008,Pocket005,Sketch009,Pad003,Sketch010,Pocket006,Sketch011,Pocket007,Sketch012,Pocket008,Sketch013,Pocket009,Chamfer001]
  Origin = -> Origin001
  Tip = -> Chamfer001
COMPONENT P2 — recipe-attached ("Dual Pipes 40 2", modeled in this document).
Construction recipe (the document's own serialized feature program — sketch geometry with constraints, then the solid features built on it; lengths are millimeters unless a unit is written):

FEATURE [Sketcher::SketchObject] Sketch014
  ArcFitTolerance = 1e-06
  AttachmentSupport = -> [XY_Plane002]
  ExternalTypes = [0]
  FullyConstrained = true
  MakeInternals = false
  MapMode = 5
  sketch-geometry (21):
    g0: LineSegment StartX=-10.5 StartY=-11.5 StartZ=0 EndX=-10.5 EndY=11.5 EndZ=0
    g1: LineSegment StartX=-10.5 StartY=11.5 StartZ=0 EndX=-8 EndY=11.5 EndZ=0
    g2: LineSegment StartX=-8 StartY=11.5 StartZ=0 EndX=-8 EndY=28.5 EndZ=0
    g3: LineSegment StartX=-8 StartY=28.5 StartZ=0 EndX=-10.5 EndY=28.5 EndZ=0
    g4: LineSegment StartX=-10.5 StartY=28.5 StartZ=0 EndX=-10.5 EndY=32.5 EndZ=0
    g5: LineSegment StartX=-10.5 StartY=32.5 StartZ=0 EndX=10.5 EndY=32.5 EndZ=0
    g6: LineSegment StartX=10.5 StartY=32.5 StartZ=0 EndX=10.5 EndY=28.5 EndZ=0
    g7: LineSegment StartX=10.5 StartY=28.5 StartZ=0 EndX=8 EndY=28.5 EndZ=0
    g8: LineSegment StartX=8 StartY=28.5 StartZ=0 EndX=8 EndY=11.5 EndZ=0
    g9: LineSegment StartX=8 StartY=11.5 StartZ=0 EndX=10.5 EndY=11.5 EndZ=0
    g10: LineSegment StartX=10.5 StartY=11.5 StartZ=0 EndX=10.5 EndY=-11.5 EndZ=0
    g11: LineSegment StartX=10.5 StartY=-11.5 StartZ=0 EndX=8 EndY=-11.5 EndZ=0
    g12: LineSegment StartX=8 StartY=-11.5 StartZ=0 EndX=8 EndY=-28.5 EndZ=0
    g13: LineSegment StartX=8 StartY=-28.5 StartZ=0 EndX=10.5 EndY=-28.5 EndZ=0
    g14: LineSegment StartX=10.5 StartY=-28.5 StartZ=0 EndX=10.5 EndY=-32.5 EndZ=0
    g15: LineSegment StartX=10.5 StartY=-32.5 StartZ=0 EndX=-10.5 EndY=-32.5 EndZ=0
    g16: LineSegment StartX=-10.5 StartY=-32.5 StartZ=0 EndX=-10.5 EndY=-28.5 EndZ=0
    g17: LineSegment StartX=-10.5 StartY=-28.5 StartZ=0 EndX=-8 EndY=-28.5 EndZ=0
    g18: LineSegment StartX=-8 StartY=-28.5 StartZ=0 EndX=-8 EndY=-11.5 EndZ=0
    g19: LineSegment StartX=-8 StartY=-11.5 StartZ=0 EndX=-10.5 EndY=-11.5 EndZ=0
    g20: Circle CenterX=0 CenterY=0 CenterZ=0 NormalX=0 NormalY=0 NormalZ=1 AngleXU=0 Radius=3
  constraints (60):
    c: Vertical(g0)
    c: Coincident(g0,g1)
    c: Coincident(g1,g2)
    c: Coincident(g2,g3)
    c: Coincident(g3,g4)
    c: Coincident(g4,g5)
    c: Coincident(g5,g6)
    c: Coincident(g6,g7)
    c: Coincident(g7,g8)
    c: Coincident(g8,g9)
    c: Horizontal(g9)
    c: Coincident(g9,g10)
    c: Coincident(g10,g11)
    c: Coincident(g11,g12)
    c: Vertical(g12)
    c: Coincident(g12,g13)
    c: Horizontal(g13)
    c: Coincident(g13,g14)
    c: Coincident(g14,g15)
    c: Horizontal(g15)
    c: Coincident(g15,g16)
    c: Coincident(g16,g17)
    c: Horizontal(g17)
    c: Coincident(g17,g18)
    c: Coincident(g18,g19)
    c: Coincident(g19,g0)
    c: Horizontal(g3)
    c: Horizontal(g1)
    c: Horizontal(g19)
    c: Horizontal(g11)
    c: Horizontal(g7)
    c: Vertical(g6)
    c: Vertical(g2)
    c: Vertical(g8)
    c: Vertical(g18)
    c: Vertical(g16)
    c: Vertical(g14)
    c: Symmetric(g4,g5,g-2)
    c: Symmetric(g9,g10,g-1)
    c: Equal(g5,g15)
    c: Equal(g7,g9)
    c: DistanceX(g2,g7) = 16  'MinorWidth'
    c: DistanceX(g5,g5) = 21  'MajorWidth'
    c: DistanceY(g15,g4) = 65  'MinorHeight'
    c: DistanceY(g2,g2) = 17  'CutoutHeight'
    c: Diameter(g20) = 6  'ScrewHoleDia'
    c: Vertical(g4)
    c: Equal(g6,g4)
    c: Equal(g4,g16)
    c: Equal(g16,g14)
    c: Symmetric(g4,g15,g-1)
    c: Equal(g3,g19)
    c: Equal(g19,g11)
    c: Equal(g11,g7)
    c: Equal(g10,g0)
    c: Equal(g2,g8)
    c: DistanceY(g0,g0) = 23
    c: Vertical(g1,g18)
    c: DistanceY(g6,g6) = 4
    c: Coincident(g20,g-1)
FEATURE [PartDesign::Pad] Pad004
  Direction = (0,0,1)
  Length = 35
  Length2 = 10
  Profile = -> Sketch014
  ReferenceAxis = -> Sketch014 [N_Axis]
  Refine = true
  Suppressed = false
  Type = 0
FEATURE [Sketcher::SketchObject] Sketch021
  ArcFitTolerance = 1e-06
  AttachmentSupport = -> [Pad004]
  ExternalTypes = [0]
  FullyConstrained = true
  MakeInternals = false
  MapMode = 5
  Placement = pos=(0,0,0) rot=(1,0,0;3.14159rad)
  sketch-geometry (1):
    g0: Circle CenterX=0 CenterY=0 CenterZ=0 NormalX=0 NormalY=0 NormalZ=1 AngleXU=0 Radius=9.25
  constraints (2):
    c: Coincident(g0,g-1)
    c: Diameter(g0) = 18.5  'PadMajorDia'
FEATURE [PartDesign::Pocket] Pocket010
  BaseFeature = -> Pad004
  Direction = (0,0,1)
  Length = 5
  Length2 = 5
  Profile = -> Sketch021
  ReferenceAxis = -> Sketch021 [N_Axis]
  Refine = true
  Suppressed = false
  Type = 0
FEATURE [Sketcher::SketchObject] Sketch022
  ArcFitTolerance = 1e-06
  AttachmentSupport = -> [Pocket010]
  ExternalTypes = [0]
  FullyConstrained = true
  MakeInternals = false
  MapMode = 5
  Placement = pos=(0,0,35) rot=(0,0,1;0rad)
  sketch-geometry (8):
    g0: LineSegment StartX=-5.25 StartY=11.068 StartZ=0 EndX=-5.25 EndY=27 EndZ=0
    g1: LineSegment StartX=-5.25 StartY=27 StartZ=0 EndX=5.25 EndY=27 EndZ=0
    g2: LineSegment StartX=5.25 StartY=27 StartZ=0 EndX=5.25 EndY=11.068 EndZ=0
    g3: LineSegment StartX=-5.25 StartY=-11.068 StartZ=0 EndX=-5.25 EndY=-27 EndZ=0
    g4: LineSegment StartX=-5.25 StartY=-27 StartZ=0 EndX=5.25 EndY=-27 EndZ=0
    g5: LineSegment StartX=5.25 StartY=-27 StartZ=0 EndX=5.25 EndY=-11.068 EndZ=0
    g6: ArcOfCircle CenterX=0 CenterY=0 CenterZ=0 NormalX=0 NormalY=0 NormalZ=1 AngleXU=0 Radius=12.25 StartAngle=1.12789 EndAngle=2.01371
    g7: ArcOfCircle CenterX=0 CenterY=0 CenterZ=0 NormalX=0 NormalY=0 NormalZ=1 AngleXU=0 Radius=12.25 StartAngle=4.26948 EndAngle=5.1553
  constraints (24):
    c: Vertical(g0)
    c: Coincident(g0,g1)
    c: Horizontal(g1)
    c: Coincident(g1,g2)
    c: Vertical(g2)
    c: Vertical(g3)
    c: Coincident(g3,g4)
    c: Horizontal(g4)
    c: Coincident(g4,g5)
    c: Vertical(g5)
    c: Coincident(g6,g0)
    c: Coincident(g6,g2)
    c: Coincident(g7,g3)
    c: Coincident(g7,g5)
    c: Coincident(g7,g6)
    c: Coincident(g7,g-1)
    c: Equal(g6,g7)
    c: Equal(g3,g5)
    c: Equal(g5,g0)
    c: Equal(g0,g2)
    c: DistanceY(g4,g1) = 54
    c: DistanceX(g1,g1) = 10.5
    c: Equal(g1,g4)
    c: Diameter(g6) = 24.5
FEATURE [PartDesign::Pad] Pad005
  BaseFeature = -> Pocket010
  Direction = (0,0,1)
  Length = 2.5
  Length2 = 10
  Profile = -> Sketch022
  ReferenceAxis = -> Sketch022 [N_Axis]
  Refine = true
  Suppressed = false
  Type = 0
FEATURE [Sketcher::SketchObject] Sketch023
  ArcFitTolerance = 1e-06
  AttachmentSupport = -> [Pad005]
  ExternalGeometry = -> [Pad005]
  ExternalTypes = [0]
  FullyConstrained = true
  MakeInternals = false
  MapMode = 5
  Placement = pos=(0,0,37.5) rot=(0,0,1;0rad)
  sketch-geometry (8):
    g0: LineSegment StartX=-3.75 StartY=14.7817 StartZ=0 EndX=-3.75 EndY=25.5 EndZ=0
    g1: LineSegment StartX=-3.75 StartY=25.5 StartZ=0 EndX=3.75 EndY=25.5 EndZ=0
    g2: LineSegment StartX=3.75 StartY=25.5 StartZ=0 EndX=3.75 EndY=14.7817 EndZ=0
    g3: LineSegment StartX=-3.75 StartY=-14.7817 StartZ=0 EndX=-3.75 EndY=-25.5 EndZ=0
    g4: LineSegment StartX=-3.75 StartY=-25.5 StartZ=0 EndX=3.75 EndY=-25.5 EndZ=0
    g5: LineSegment StartX=3.75 StartY=-25.5 StartZ=0 EndX=3.75 EndY=-14.7817 EndZ=0
    g6: ArcOfCircle CenterX=0 CenterY=0 CenterZ=0 NormalX=0 NormalY=0 NormalZ=1 AngleXU=0 Radius=15.25 StartAngle=4.46394 EndAngle=4.96084
    g7: ArcOfCircle CenterX=0 CenterY=0 CenterZ=0 NormalX=0 NormalY=0 NormalZ=1 AngleXU=0 Radius=15.25 StartAngle=1.32235 EndAngle=1.81925
  constraints (24):
    c: Vertical(g0)
    c: Coincident(g0,g1)
    c: Horizontal(g1)
    c: Coincident(g1,g2)
    c: Vertical(g2)
    c: Vertical(g3)
    c: Coincident(g3,g4)
    c: Horizontal(g4)
    c: Coincident(g4,g5)
    c: Coincident(g6,g3)
    c: Coincident(g6,g5)
    c: Coincident(g7,g0)
    c: Coincident(g7,g2)
    c: Coincident(g6,g7)
    c: Coincident(g6,g-1)
    c: Vertical(g5)
    c: Equal(g5,g3)
    c: Equal(g3,g0)
    c: Equal(g0,g2)
    c: Equal(g1,g4)
    c: Equal(g6,g7)
    c: DistanceY(g1,g-3) = 1.5
    c: DistanceX(g1,g-3) = 1.5
    c: Diameter(g6) = 30.5
FEATURE [PartDesign::Pocket] Pocket011
  BaseFeature = -> Pad005
  Direction = (0,0,-1)
  Length = 5
  Length2 = 5
  Profile = -> Sketch023
  ReferenceAxis = -> Sketch023 [N_Axis]
  Refine = true
  Suppressed = false
  Type = 1
FEATURE [Sketcher::SketchObject] Sketch024
  ArcFitTolerance = 1e-06
  AttachmentSupport = -> [Pocket011]
  ExternalTypes = [0]
  FullyConstrained = true
  MakeInternals = false
  MapMode = 5
  Placement = pos=(0,0,35) rot=(0,0,1;0rad)
  expr: Constraints[1] = <<Sketch021>>.Constraints.PadMajorDia
  sketch-geometry (1):
    g0: Circle CenterX=0 CenterY=0 CenterZ=0 NormalX=0 NormalY=0 NormalZ=1 AngleXU=0 Radius=9.25
  constraints (2):
    c: Coincident(g0,g-1)
    c: Diameter(g0) = 18.5
FEATURE [PartDesign::Pocket] Pocket012
  BaseFeature = -> Pocket011
  Direction = (0,0,-1)
  Length = 0
  Length2 = 5
  Offset = 5
  Profile = -> Sketch024
  ReferenceAxis = -> Sketch024 [N_Axis]
  Refine = true
  Suppressed = false
  Type = 3
  UpToFace = -> Pocket011 [Face43]
FEATURE [Sketcher::SketchObject] Sketch025
  ArcFitTolerance = 1e-06
  AttachmentSupport = -> [Pocket012]
  ExternalGeometry = -> [Pocket012]
  ExternalTypes = [0]
  FullyConstrained = true
  MakeInternals = false
  MapMode = 5
  Placement = pos=(-10.5,0,0) rot=(0.57735,-0.57735,-0.57735;2.0944rad)
  sketch-geometry (8):
    g0: LineSegment StartX=-9.25 StartY=10 StartZ=0 EndX=9.25 EndY=10 EndZ=0
    g1: LineSegment StartX=9.25 StartY=10 StartZ=0 EndX=9.25 EndY=23.5 EndZ=0
    g2: LineSegment StartX=9.25 StartY=23.5 StartZ=0 EndX=5 EndY=23.5 EndZ=0
    g3: LineSegment StartX=5 StartY=23.5 StartZ=0 EndX=5 EndY=30 EndZ=0
    g4: LineSegment StartX=5 StartY=30 StartZ=0 EndX=-5 EndY=30 EndZ=0
    g5: LineSegment StartX=-5 StartY=30 StartZ=0 EndX=-5 EndY=23.5 EndZ=0
    g6: LineSegment StartX=-5 StartY=23.5 StartZ=0 EndX=-9.25 EndY=23.5 EndZ=0
    g7: LineSegment StartX=-9.25 StartY=23.5 StartZ=0 EndX=-9.25 EndY=10 EndZ=0
  constraints (25):
    c: Coincident(g-3,g0)
    c: Coincident(g0,g-3)
    c: Coincident(g0,g1)
    c: Vertical(g1)
    c: Coincident(g1,g2)
    c: Coincident(g2,g3)
    c: Vertical(g3)
    c: Coincident(g3,g4)
    c: Horizontal(g4)
    c: Coincident(g4,g5)
    c: Coincident(g5,g6)
    c: Horizontal(g6)
    c: Coincident(g6,g7)
    c: Coincident(g7,g0)
    c: Vertical(g7)
    c: Horizontal(g2)
    c: Vertical(g5)
    c: Equal(g7,g1)
    c: DistanceY(g0,g-4) = 25  'Space'
    c: DistanceX(g4,g4) = 10  'SlotWidth'
    c: DistanceY(g1,g1) = 13.5  'PlugHeight'
    c: DistanceY(g3,g-4) = 5
    c: Equal(g2,g6)
    c: DistanceY(g1,g-4) = 11.5
    c: DistanceY(g3,g3) = 6.5  'SlotHeight'
FEATURE [PartDesign::Pocket] Pocket013
  BaseFeature = -> Pocket012
  Direction = (1,0,0)
  Length = 5
  Length2 = 5
  Profile = -> Sketch025
  ReferenceAxis = -> Sketch025 [N_Axis]
  Refine = true
  Suppressed = false
  Type = 1
FEATURE [PartDesign::Chamfer] Chamfer002
  Angle = 45
  Base = -> Pocket013 [Edge155]
  BaseFeature = -> Pocket013
  ChamferType = 0
  FlipDirection = false
  Refine = true
  Size = 3
  Size2 = 1
  SupportTransform = false
  Suppressed = false
  UseAllEdges = false
FEATURE [PartDesign::CoordinateSystem] Mount
  AttacherType = Attacher::AttachEngine3D
  AttachmentSupport = -> [Chamfer002]
  MapMode = 11
  Placement = pos=(0,0,0) rot=(0.707107,-0.707107,0;3.14159rad)
FEATURE [PartDesign::CoordinateSystem] Plug  label="Plug001"
  AttacherType = Attacher::AttachEngine3D
  AttachmentSupport = -> [Chamfer002]
  MapMode = 45
  Placement = pos=(0,3.8878e-11,30) rot=(0,0,1;1.5708rad)
FEATURE [PartDesign::Body] Body002  label="Dual Pipes 40 2"
  AllowCompound = false
  Group = -> [Sketch014,Pad004,Sketch021,Pocket010,Sketch022,Pad005,Sketch023,Pocket011,Sketch024,Pocket012,Sketch025,Pocket013,Chamfer002,Mount,Plug]
  Origin = -> Origin002
  Tip = -> Chamfer002
COMPONENT P3 — recipe-attached ("Plug", modeled in this document).
Construction recipe (the document's own serialized feature program — sketch geometry with constraints, then the solid features built on it; lengths are millimeters unless a unit is written):

FEATURE [Sketcher::SketchObject] Sketch026
  ArcFitTolerance = 1e-06
  AttachmentSupport = -> [XY_Plane003]
  ExternalTypes = [0]
  FullyConstrained = true
  MakeInternals = false
  MapMode = 5
  expr: .Constraints.PlugDia = <<Sketch021>>.Constraints.PadMajorDia - 1 mm
  expr: Constraints[21] = <<Sketch014>>.Constraints.MajorWidth
  expr: Constraints[23] = <<Sketch025>>.Constraints.SlotWidth - 1 mm
  sketch-geometry (8):
    g0: LineSegment StartX=-7.50417 StartY=4.5 StartZ=0 EndX=-10.5 EndY=4.5 EndZ=0
    g1: LineSegment StartX=-10.5 StartY=4.5 StartZ=0 EndX=-10.5 EndY=-4.5 EndZ=0
    g2: LineSegment StartX=-10.5 StartY=-4.5 StartZ=0 EndX=-7.50417 EndY=-4.5 EndZ=0
    g3: LineSegment StartX=7.50417 StartY=4.5 StartZ=0 EndX=10.5 EndY=4.5 EndZ=0
    g4: LineSegment StartX=10.5 StartY=4.5 StartZ=0 EndX=10.5 EndY=-4.5 EndZ=0
    g5: LineSegment StartX=10.5 StartY=-4.5 StartZ=0 EndX=7.50417 EndY=-4.5 EndZ=0
    g6: ArcOfCircle CenterX=0 CenterY=0 CenterZ=0 NormalX=0 NormalY=0 NormalZ=1 AngleXU=0 Radius=8.75 StartAngle=0.540175 EndAngle=2.60142
    g7: ArcOfCircle CenterX=0 CenterY=0 CenterZ=0 NormalX=0 NormalY=0 NormalZ=1 AngleXU=0 Radius=8.75 StartAngle=3.68177 EndAngle=5.74301
  constraints (24):
    c: Horizontal(g0)
    c: Coincident(g0,g1)
    c: Vertical(g1)
    c: Coincident(g1,g2)
    c: Horizontal(g2)
    c: Horizontal(g3)
    c: Coincident(g3,g4)
    c: Vertical(g4)
    c: Coincident(g4,g5)
    c: Horizontal(g5)
    c: Coincident(g6,g0)
    c: Coincident(g6,g3)
    c: Coincident(g7,g2)
    c: Coincident(g7,g5)
    c: Coincident(g7,g6)
    c: Coincident(g7,g-1)
    c: Equal(g6,g7)
    c: Equal(g0,g2)
    c: Equal(g2,g5)
    c: Equal(g5,g3)
    c: Equal(g4,g1)
    c: DistanceX(g0,g3) = 21
    c: Diameter(g7) = 17.5  'PlugDia'
    c: DistanceY(g1,g1) = 9
FEATURE [PartDesign::Pad] Pad006
  Direction = (0,0,1)
  Length = 12.5
  Length2 = 10
  Profile = -> Sketch026
  ReferenceAxis = -> Sketch026 [N_Axis]
  Refine = true
  Suppressed = false
  Type = 0
  expr: Length = <<Sketch025>>.Constraints.PlugHeight - 1 mm
FEATURE [Sketcher::SketchObject] Sketch027
  ArcFitTolerance = 1e-06
  AttachmentSupport = -> [Pad006]
  ExternalGeometry = -> [Pad006]
  ExternalTypes = [0]
  FullyConstrained = true
  MakeInternals = false
  MapMode = 5
  Placement = pos=(0,0,12.5) rot=(0,0,1;0rad)
  sketch-geometry (8):
    g0: ArcOfCircle CenterX=1e-16 CenterY=3e-16 CenterZ=0 NormalX=0 NormalY=0 NormalZ=1 AngleXU=0 Radius=8.75 StartAngle=2.60142 EndAngle=3.68177
    g1: ArcOfCircle CenterX=-7e-16 CenterY=-3e-16 CenterZ=0 NormalX=0 NormalY=0 NormalZ=1 AngleXU=0 Radius=8.75 StartAngle=5.74301 EndAngle=6.82336
    g2: LineSegment StartX=-7.50417 StartY=4.5 StartZ=0 EndX=-10.5 EndY=4.50002 EndZ=0
    g3: LineSegment StartX=-10.5 StartY=4.50002 StartZ=0 EndX=-10.5 EndY=-4.5 EndZ=0
    g4: LineSegment StartX=-10.5 StartY=-4.5 StartZ=0 EndX=-7.50417 EndY=-4.5 EndZ=0
    g5: LineSegment StartX=7.50417 StartY=4.5 StartZ=0 EndX=10.5 EndY=4.5 EndZ=0
    g6: LineSegment StartX=10.5 StartY=4.5 StartZ=0 EndX=10.5 EndY=-4.5 EndZ=0
    g7: LineSegment StartX=10.5 StartY=-4.5 StartZ=0 EndX=7.50417 EndY=-4.5 EndZ=0
  constraints (21):
    c: Coincident(g1,g-3)
    c: Coincident(g1,g-4)
    c: Coincident(g1,g5)
    c: Coincident(g5,g6)
    c: Vertical(g6)
    c: Coincident(g6,g7)
    c: Coincident(g7,g1)
    c: Horizontal(g7)
    c: Equal(g7,g4)
    c: Coincident(g3,g2)
    c: Coincident(g4,g3)
    c: Vertical(g3)
    c: Equal(g5,g2)
    c: Coincident(g5,g-5)
    c: Equal(g1,g0)
    c: Equal(g0,g-3)
    c: Coincident(g0,g-3)
    c: Coincident(g0,g-4)
    c: Coincident(g4,g0)
    c: Coincident(g2,g0)
    c: Horizontal(g4)
FEATURE [PartDesign::Pocket] Pocket014
  BaseFeature = -> Pad006
  Direction = (0,0,-1)
  Length = 0
  Length2 = 5
  Offset = -5
  Profile = -> Sketch027
  ReferenceAxis = -> Sketch027 [N_Axis]
  Refine = true
  Suppressed = false
  Type = 3
  UpToFace = -> Pad006 [Face9]
  expr: Offset = -<<Sketch025>>.Constraints.SlotHeight + 1.5 mm
FEATURE [Sketcher::SketchObject] Sketch028
  ArcFitTolerance = 1e-06
  AttachmentSupport = -> [Pocket014]
  ExternalTypes = [0]
  FullyConstrained = true
  MakeInternals = false
  MapMode = 5
  Placement = pos=(0,0,12.5) rot=(0,0,1;0rad)
  expr: Constraints[40] = <<Sketch026>>.Constraints.PlugDia - 3 mm
  sketch-geometry (17):
    g0: Circle CenterX=0 CenterY=0 CenterZ=0 NormalX=0 NormalY=0 NormalZ=1 AngleXU=0 Radius=2
    g1: LineSegment StartX=-1.5 StartY=7.09313 StartZ=0 EndX=-1.5 EndY=3.16228 EndZ=0
    g2: LineSegment StartX=1.5 StartY=7.09313 StartZ=0 EndX=1.5 EndY=3.16228 EndZ=0
    g3: LineSegment StartX=3.16228 StartY=1.5 StartZ=0 EndX=7.09313 EndY=1.5 EndZ=0
    g4: LineSegment StartX=3.16228 StartY=-1.5 StartZ=0 EndX=7.09313 EndY=-1.5 EndZ=0
    g5: LineSegment StartX=1.5 StartY=-3.16228 StartZ=0 EndX=1.5 EndY=-7.09313 EndZ=0
    g6: LineSegment StartX=-1.5 StartY=-3.16228 StartZ=0 EndX=-1.5 EndY=-7.09313 EndZ=0
    g7: LineSegment StartX=-3.16228 StartY=-1.5 StartZ=0 EndX=-7.09313 EndY=-1.5 EndZ=0
    g8: LineSegment StartX=-7.09313 StartY=1.5 StartZ=0 EndX=-3.16228 EndY=1.5 EndZ=0
    g9: ArcOfCircle CenterX=0 CenterY=0 CenterZ=0 NormalX=0 NormalY=0 NormalZ=1 AngleXU=0 Radius=3.5 StartAngle=2.01371 EndAngle=2.69868
    g10: ArcOfCircle CenterX=0 CenterY=0 CenterZ=0 NormalX=0 NormalY=0 NormalZ=1 AngleXU=0 Radius=7.25 StartAngle=1.7792 EndAngle=2.93319
    g11: ArcOfCircle CenterX=0 CenterY=0 CenterZ=0 NormalX=0 NormalY=0 NormalZ=1 AngleXU=0 Radius=3.5 StartAngle=0.442911 EndAngle=1.12789
    g12: ArcOfCircle CenterX=0 CenterY=0 CenterZ=0 NormalX=0 NormalY=0 NormalZ=1 AngleXU=0 Radius=7.25 StartAngle=0.208402 EndAngle=1.36239
    g13: ArcOfCircle CenterX=0 CenterY=0 CenterZ=0 NormalX=0 NormalY=0 NormalZ=1 AngleXU=0 Radius=3.5 StartAngle=5.1553 EndAngle=5.84027
    g14: ArcOfCircle CenterX=0 CenterY=0 CenterZ=0 NormalX=0 NormalY=0 NormalZ=1 AngleXU=0 Radius=7.25 StartAngle=4.92079 EndAngle=6.07478
    g15: ArcOfCircle CenterX=0 CenterY=0 CenterZ=0 NormalX=0 NormalY=0 NormalZ=1 AngleXU=0 Radius=3.5 StartAngle=3.5845 EndAngle=4.26948
    g16: ArcOfCircle CenterX=0 CenterY=0 CenterZ=0 NormalX=0 NormalY=0 NormalZ=1 AngleXU=0 Radius=7.25 StartAngle=3.34999 EndAngle=4.50399
  constraints (50):
    c: Coincident(g0,g-1)
    c: Diameter(g0) = 4
    c: Horizontal(g4)
    c: Vertical(g5)
    c: Vertical(g6)
    c: Horizontal(g7)
    c: Horizontal(g8)
    c: Vertical(g1)
    c: Vertical(g2)
    c: Horizontal(g3)
    c: Coincident(g9,g8)
    c: Coincident(g9,g1)
    c: Coincident(g10,g1)
    c: Coincident(g10,g8)
    c: Coincident(g11,g2)
    c: Coincident(g11,g3)
    c: Coincident(g12,g2)
    c: Coincident(g12,g3)
    c: Coincident(g13,g4)
    c: Coincident(g13,g5)
    c: Coincident(g14,g5)
    c: Coincident(g14,g4)
    c: Coincident(g15,g6)
    c: Coincident(g15,g7)
    c: Coincident(g16,g6)
    c: Coincident(g16,g7)
    c: Coincident(g11,g15)
    c: Coincident(g11,g16)
    c: Coincident(g11,g12)
    c: Coincident(g11,g13)
    c: Coincident(g11,g0)
    c: Coincident(g14,g9)
    c: Coincident(g14,g10)
    c: Coincident(g14,g0)
    c: Equal(g12,g10)
    c: Equal(g10,g16)
    c: Equal(g16,g14)
    c: Equal(g13,g15)
    c: Equal(g15,g9)
    c: Equal(g9,g11)
    c: Diameter(g12) = 14.5
    c: Diameter(g11) = 7
    c: DistanceX(g1,g2) = 3
    c: DistanceY(g7,g8) = 3
    c: Horizontal(g3,g8)
    c: Vertical(g6,g1)
    c: Vertical(g2,g5)
    c: Horizontal(g5,g6)
    c: Horizontal(g4,g7)
    c: Equal(g4,g5)
FEATURE [PartDesign::Pocket] Pocket015
  BaseFeature = -> Pocket014
  Direction = (0,0,-1)
  Length = 5
  Length2 = 5
  Profile = -> Sketch028
  ReferenceAxis = -> Sketch028 [N_Axis]
  Refine = true
  Suppressed = false
  Type = 1
FEATURE [PartDesign::CoordinateSystem] Mount001
  AttacherType = Attacher::AttachEngine3D
  AttachmentSupport = -> [Pocket015]
  MapMode = 45
  Placement = pos=(-9.45603e-06,4.05261e-06,5) rot=(0,0,1;1.5708rad)
FEATURE [PartDesign::Body] Body003  label="Plug"
  AllowCompound = false
  Group = -> [Sketch026,Pad006,Sketch027,Pocket014,Sketch028,Pocket015,Mount001]
  Origin = -> Origin003
  Tip = -> Pocket015
COMPONENT P4 — recipe-attached ("Dual Pipes 29mm", modeled in this document).
Construction recipe (the document's own serialized feature program — sketch geometry with constraints, then the solid features built on it; lengths are millimeters unless a unit is written):

FEATURE [Sketcher::SketchObject] Sketch029
  ArcFitTolerance = 1e-06
  AttachmentSupport = -> [XY_Plane007]
  ExternalTypes = [0]
  FullyConstrained = true
  MakeInternals = false
  MapMode = 5
  sketch-geometry (32):
    g0: LineSegment StartX=-10 StartY=27 StartZ=0 EndX=-10 EndY=23 EndZ=0
    g1: LineSegment StartX=-10 StartY=23 StartZ=0 EndX=-8 EndY=23 EndZ=0
    g2: LineSegment StartX=-8 StartY=23 StartZ=0 EndX=-8 EndY=6 EndZ=0
    g3: LineSegment StartX=-8 StartY=6 StartZ=0 EndX=-10 EndY=6 EndZ=0
    g4: LineSegment StartX=-10 StartY=-6 StartZ=0 EndX=-8 EndY=-6 EndZ=0
    g5: LineSegment StartX=-8 StartY=-6 StartZ=0 EndX=-8 EndY=-23 EndZ=0
    g6: LineSegment StartX=-8 StartY=-23 StartZ=0 EndX=-10 EndY=-23 EndZ=0
    g7: LineSegment StartX=-10 StartY=-23 StartZ=0 EndX=-10 EndY=-27 EndZ=0
    g8: LineSegment StartX=-10 StartY=-27 StartZ=0 EndX=10 EndY=-27 EndZ=0
    g9: LineSegment StartX=10 StartY=-27 StartZ=0 EndX=10 EndY=-23 EndZ=0
    g10: LineSegment StartX=10 StartY=-23 StartZ=0 EndX=8 EndY=-23 EndZ=0
    g11: LineSegment StartX=8 StartY=-23 StartZ=0 EndX=8 EndY=-6 EndZ=0
    g12: LineSegment StartX=8 StartY=-6 StartZ=0 EndX=10 EndY=-6 EndZ=0
    g13: LineSegment StartX=10 StartY=6 StartZ=0 EndX=8 EndY=6 EndZ=0
    g14: LineSegment StartX=8 StartY=6 StartZ=0 EndX=8 EndY=23 EndZ=0
    g15: LineSegment StartX=8 StartY=23 StartZ=0 EndX=10 EndY=23 EndZ=0
    g16: LineSegment StartX=10 StartY=23 StartZ=0 EndX=10 EndY=27 EndZ=0
    g17: LineSegment StartX=10 StartY=27 StartZ=0 EndX=-10 EndY=27 EndZ=0
    g18: Circle CenterX=0 CenterY=14.5 CenterZ=0 NormalX=0 NormalY=0 NormalZ=1 AngleXU=0 Radius=2
    g19: Circle CenterX=0 CenterY=-14.5 CenterZ=0 NormalX=0 NormalY=0 NormalZ=1 AngleXU=0 Radius=2
    g20: LineSegment [constr] StartX=0 StartY=14.5 StartZ=0 EndX=-8 EndY=14.5 EndZ=0
    g21: LineSegment StartX=-10 StartY=6 StartZ=0 EndX=-10 EndY=2 EndZ=0
    g22: LineSegment StartX=-10 StartY=2 StartZ=0 EndX=-8 EndY=2 EndZ=0
    g23: LineSegment StartX=-8 StartY=2 StartZ=0 EndX=-8 EndY=-2 EndZ=0
    g24: LineSegment StartX=-8 StartY=-2 StartZ=0 EndX=-10 EndY=-2 EndZ=0
    g25: LineSegment StartX=-10 StartY=-2 StartZ=0 EndX=-10 EndY=-6 EndZ=0
    g26: LineSegment StartX=10 StartY=-6 StartZ=0 EndX=10 EndY=-2 EndZ=0
    g27: LineSegment StartX=10 StartY=-2 StartZ=0 EndX=8 EndY=-2 EndZ=0
    g28: LineSegment StartX=8 StartY=-2 StartZ=0 EndX=8 EndY=2 EndZ=0
    g29: LineSegment StartX=8 StartY=2 StartZ=0 EndX=10 EndY=2 EndZ=0
    g30: LineSegment StartX=10 StartY=2 StartZ=0 EndX=10 EndY=6 EndZ=0
    g31: Circle CenterX=0 CenterY=0 CenterZ=0 NormalX=0 NormalY=0 NormalZ=1 AngleXU=0 Radius=3
  constraints (90):
    c: Vertical(g0)
    c: Coincident(g0,g1)
    c: Coincident(g1,g2)
    c: Vertical(g2)
    c: Coincident(g2,g3)
    c: Horizontal(g3)
    c: Horizontal(g4)
    c: Coincident(g4,g5)
    c: Coincident(g5,g6)
    c: Horizontal(g6)
    c: Coincident(g6,g7)
    c: Vertical(g7)
    c: Coincident(g7,g8)
    c: Horizontal(g8)
    c: Coincident(g8,g9)
    c: Coincident(g9,g10)
    c: Coincident(g10,g11)
    c: Coincident(g11,g12)
    c: Coincident(g13,g14)
    c: Vertical(g14)
    c: Coincident(g14,g15)
    c: Horizontal(g15)
    c: Coincident(g15,g16)
    c: Coincident(g16,g17)
    c: Coincident(g17,g0)
    c: Horizontal(g1)
    c: Horizontal(g13)
    c: Horizontal(g12)
    c: Horizontal(g10)
    c: Vertical(g5)
    c: Vertical(g16)
    c: Vertical(g11)
    c: Vertical(g9)
    c: Symmetric(g8,g16,g-1)
    c: Symmetric(g3,g4,g-1)
    c: Symmetric(g0,g16,g-2)
    c: Vertical(g0,g3)
    c: Vertical(g3,g6)
    c: Vertical(g13,g9)
    c: Equal(g9,g7)
    c: Equal(g7,g0)
    c: Equal(g0,g16)
    c: Equal(g15,g3)
    c: Equal(g13,g12)
    c: Equal(g12,g4)
    c: DistanceX(g17,g17) = 20
    c: DistanceX(g1,g14) = 16
    c: PointOnObject(g18,g-2)
    c: Equal(g19,g18)
    c: Symmetric(g19,g18,g-1)
    c: Diameter(g18) = 4  'ScrewHoleDia'
    c: DistanceY(g2,g2) = 17
    c: Coincident(g20,g18)
    c: Symmetric(g2,g2,g20)
    c: Horizontal(g20)
    c: DistanceY(g16,g16) = 4
    c: DistanceY(g19,g18) = 29
    c: Equal(g14,g2)
    c: Equal(g5,g11)
    c: Coincident(g3,g21)
    c: Vertical(g21)
    c: Coincident(g21,g22)
    c: Coincident(g22,g23)
    c: Vertical(g23)
    c: Coincident(g23,g24)
    c: Horizontal(g24)
    c: Coincident(g24,g25)
    c: Coincident(g25,g4)
    c: Coincident(g12,g26)
    c: Coincident(g26,g27)
    c: Coincident(g27,g28)
    c: Vertical(g28)
    c: Coincident(g28,g29)
    c: Coincident(g29,g30)
    c: Coincident(g30,g13)
    c: Vertical(g30)
    c: Vertical(g25)
    c: Vertical(g26)
    c: Horizontal(g27)
    c: Horizontal(g22)
    c: Horizontal(g29)
    c: Equal(g0,g21)
    c: Equal(g21,g30)
    c: Equal(g30,g26)
    c: Equal(g26,g25)
    c: Vertical(g28,g13)
    c: Vertical(g22,g2)
    c: Vertical(g26,g29)
    c: Coincident(g31,g-1)
    c: Diameter(g31) = 6
FEATURE [PartDesign::Pad] Pad007
  Direction = (0,0,1)
  Length = 35
  Length2 = 10
  Profile = -> Sketch029
  ReferenceAxis = -> Sketch029 [N_Axis]
  Refine = true
  Suppressed = false
  Type = 0
FEATURE [Sketcher::SketchObject] Sketch030
  ArcFitTolerance = 1e-06
  AttachmentSupport = -> [Pad007]
  ExternalGeometry = -> [Pad007]
  ExternalTypes = [0]
  FullyConstrained = true
  MakeInternals = false
  MapMode = 5
  Placement = pos=(0,0,0) rot=(1,0,0;3.14159rad)
  sketch-geometry (2):
    g0: Circle CenterX=0 CenterY=14.5 CenterZ=0 NormalX=0 NormalY=0 NormalZ=1 AngleXU=0 Radius=9.25
    g1: Circle CenterX=0 CenterY=-14.5 CenterZ=0 NormalX=0 NormalY=0 NormalZ=1 AngleXU=0 Radius=9.25
  constraints (4):
    c: Coincident(g0,g-3)
    c: Coincident(g1,g-4)
    c: Equal(g1,g0)
    c: Diameter(g0) = 18.5
FEATURE [PartDesign::Pocket] Pocket016
  BaseFeature = -> Pad007
  Direction = (0,0,1)
  Length = 3
  Length2 = 5
  Profile = -> Sketch030
  ReferenceAxis = -> Sketch030 [N_Axis]
  Refine = true
  Suppressed = false
  Type = 0
FEATURE [Sketcher::SketchObject] Sketch031
  ArcFitTolerance = 1e-06
  AttachmentSupport = -> [Pocket016]
  ExternalGeometry = -> [Pocket016]
  ExternalTypes = [0]
  FullyConstrained = true
  MakeInternals = false
  MapMode = 5
  Placement = pos=(0,0,35) rot=(0,0,1;0rad)
  sketch-geometry (10):
    g0: LineSegment StartX=-8 StartY=18.0444 StartZ=0 EndX=-8 EndY=10.9556 EndZ=0
    g1: LineSegment StartX=8 StartY=18.0444 StartZ=0 EndX=8 EndY=10.9556 EndZ=0
    g2: LineSegment StartX=-8 StartY=-10.9556 StartZ=0 EndX=-8 EndY=-18.0444 EndZ=0
    g3: LineSegment StartX=8 StartY=-10.9556 StartZ=0 EndX=8 EndY=-18.0444 EndZ=0
    g4: ArcOfCircle CenterX=0 CenterY=14.5 CenterZ=0 NormalX=0 NormalY=0 NormalZ=1 AngleXU=0 Radius=8.75 StartAngle=0.417055 EndAngle=2.72454
    g5: ArcOfCircle CenterX=0 CenterY=14.5 CenterZ=0 NormalX=0 NormalY=0 NormalZ=1 AngleXU=0 Radius=8.75 StartAngle=3.55865 EndAngle=5.86613
    g6: ArcOfCircle CenterX=0 CenterY=-14.5 CenterZ=0 NormalX=0 NormalY=0 NormalZ=1 AngleXU=0 Radius=8.75 StartAngle=0.417055 EndAngle=2.72454
    g7: ArcOfCircle CenterX=0 CenterY=-14.5 CenterZ=0 NormalX=0 NormalY=0 NormalZ=1 AngleXU=0 Radius=8.75 StartAngle=3.55865 EndAngle=5.86613
    g8: Circle CenterX=0 CenterY=14.5 CenterZ=0 NormalX=0 NormalY=0 NormalZ=1 AngleXU=0 Radius=2
    g9: Circle CenterX=0 CenterY=-14.5 CenterZ=0 NormalX=0 NormalY=0 NormalZ=1 AngleXU=0 Radius=2
  constraints (28):
    c: Equal(g0,g1)
    c: Equal(g1,g3)
    c: Coincident(g5,g4)
    c: Coincident(g8,g4)
    c: Coincident(g1,g4)
    c: Coincident(g0,g4)
    c: Coincident(g0,g5)
    c: Coincident(g1,g5)
    c: Vertical(g0)
    c: Vertical(g2)
    c: Vertical(g3)
    c: Coincident(g4,g-3)
    c: Vertical(g0,g-5)
    c: Coincident(g6,g3)
    c: Coincident(g7,g3)
    c: Coincident(g6,g2)
    c: Coincident(g2,g7)
    c: Coincident(g6,g-4)
    c: Coincident(g7,g6)
    c: Coincident(g9,g6)
    c: Equal(g7,g6)
    c: Equal(g6,g5)
    c: Equal(g5,g4)
    c: Equal(g2,g3)
    c: Equal(g9,g8)
    c: Equal(g8,g-3)
    c: Diameter(g4) = 17.5  'PadMinorDia'
    c: Vertical(g1)
FEATURE [PartDesign::Pad] Pad008
  BaseFeature = -> Pocket016
  Direction = (0,0,1)
  Length = 2.5
  Length2 = 10
  Profile = -> Sketch031
  ReferenceAxis = -> Sketch031 [N_Axis]
  Refine = true
  Suppressed = false
  Type = 0
FEATURE [Sketcher::SketchObject] Sketch032
  ArcFitTolerance = 1e-06
  AttachmentSupport = -> [Pad008]
  ExternalGeometry = -> [Pad008]
  ExternalTypes = [0]
  FullyConstrained = true
  MakeInternals = false
  MapMode = 5
  Placement = pos=(0,0,37.5) rot=(0,0,1;0rad)
  expr: Constraints[45] = <<Sketch029>>.Constraints.ScrewHoleDia + .Constraints.WallThickness * 2
  expr: Constraints[46] = <<Sketch031>>.Constraints.PadMinorDia - .Constraints.WallThickness * 2
  sketch-geometry (32):
    g0: ArcOfCircle CenterX=0 CenterY=14.5 CenterZ=0 NormalX=0 NormalY=0 NormalZ=1 AngleXU=0 Radius=6.25 StartAngle=1.77215 EndAngle=2.94023
    g1: ArcOfCircle CenterX=0 CenterY=14.5 CenterZ=0 NormalX=0 NormalY=0 NormalZ=1 AngleXU=0 Radius=4.5 StartAngle=1.85228 EndAngle=2.86011
    g2: ArcOfCircle CenterX=0 CenterY=14.5 CenterZ=0 NormalX=0 NormalY=0 NormalZ=1 AngleXU=0 Radius=6.25 StartAngle=0.201358 EndAngle=1.36944
    g3: ArcOfCircle CenterX=0 CenterY=14.5 CenterZ=0 NormalX=0 NormalY=0 NormalZ=1 AngleXU=0 Radius=4.5 StartAngle=0.28148 EndAngle=1.28932
    g4: ArcOfCircle CenterX=0 CenterY=14.5 CenterZ=0 NormalX=0 NormalY=0 NormalZ=1 AngleXU=0 Radius=4.5 StartAngle=4.99387 EndAngle=6.00171
    g5: ArcOfCircle CenterX=0 CenterY=14.5 CenterZ=0 NormalX=0 NormalY=0 NormalZ=1 AngleXU=0 Radius=6.25 StartAngle=4.91375 EndAngle=6.08183
    g6: ArcOfCircle CenterX=0 CenterY=14.5 CenterZ=0 NormalX=0 NormalY=0 NormalZ=1 AngleXU=0 Radius=4.5 StartAngle=3.42307 EndAngle=4.43091
    g7: ArcOfCircle CenterX=0 CenterY=14.5 CenterZ=0 NormalX=0 NormalY=0 NormalZ=1 AngleXU=0 Radius=6.25 StartAngle=3.34295 EndAngle=4.51103
    g8: LineSegment StartX=-4.3229 StartY=13.25 StartZ=0 EndX=-6.12372 EndY=13.25 EndZ=0
    g9: LineSegment StartX=-6.12372 StartY=15.75 StartZ=0 EndX=-4.3229 EndY=15.75 EndZ=0
    g10: LineSegment StartX=-1.25 StartY=18.8229 StartZ=0 EndX=-1.25 EndY=20.6237 EndZ=0
    g11: LineSegment StartX=1.25 StartY=18.8229 StartZ=0 EndX=1.25 EndY=20.6237 EndZ=0
    g12: LineSegment StartX=4.3229 StartY=15.75 StartZ=0 EndX=6.12372 EndY=15.75 EndZ=0
    g13: LineSegment StartX=4.3229 StartY=13.25 StartZ=0 EndX=6.12372 EndY=13.25 EndZ=0
    g14: LineSegment StartX=1.25 StartY=10.1771 StartZ=0 EndX=1.25 EndY=8.37628 EndZ=0
    g15: LineSegment StartX=-1.25 StartY=8.37628 StartZ=0 EndX=-1.25 EndY=10.1771 EndZ=0
    g16: ArcOfCircle CenterX=0 CenterY=-14.5 CenterZ=0 NormalX=0 NormalY=0 NormalZ=1 AngleXU=0 Radius=6.25 StartAngle=3.34295 EndAngle=4.51103
    g17: ArcOfCircle CenterX=0 CenterY=-14.5 CenterZ=0 NormalX=0 NormalY=0 NormalZ=1 AngleXU=0 Radius=4.5 StartAngle=3.42307 EndAngle=4.43091
    g18: ArcOfCircle CenterX=0 CenterY=-14.5 CenterZ=0 NormalX=0 NormalY=0 NormalZ=1 AngleXU=0 Radius=6.25 StartAngle=4.91375 EndAngle=6.08183
    g19: ArcOfCircle CenterX=0 CenterY=-14.5 CenterZ=0 NormalX=0 NormalY=0 NormalZ=1 AngleXU=0 Radius=4.5 StartAngle=4.99387 EndAngle=6.00171
    g20: ArcOfCircle CenterX=0 CenterY=-14.5 CenterZ=0 NormalX=0 NormalY=0 NormalZ=1 AngleXU=0 Radius=4.5 StartAngle=0.28148 EndAngle=1.28932
    g21: ArcOfCircle CenterX=0 CenterY=-14.5 CenterZ=0 NormalX=0 NormalY=0 NormalZ=1 AngleXU=0 Radius=6.25 StartAngle=0.201358 EndAngle=1.36944
    g22: ArcOfCircle CenterX=0 CenterY=-14.5 CenterZ=0 NormalX=0 NormalY=0 NormalZ=1 AngleXU=0 Radius=4.5 StartAngle=1.85228 EndAngle=2.86011
    g23: ArcOfCircle CenterX=0 CenterY=-14.5 CenterZ=0 NormalX=0 NormalY=0 NormalZ=1 AngleXU=0 Radius=6.25 StartAngle=1.77215 EndAngle=2.94023
    g24: LineSegment StartX=-4.3229 StartY=-13.25 StartZ=0 EndX=-6.12372 EndY=-13.25 EndZ=0
    g25: LineSegment StartX=-6.12372 StartY=-15.75 StartZ=0 EndX=-4.3229 EndY=-15.75 EndZ=0
    g26: LineSegment StartX=-1.25 StartY=-18.8229 StartZ=0 EndX=-1.25 EndY=-20.6237 EndZ=0
    g27: LineSegment StartX=1.25 StartY=-18.8229 StartZ=0 EndX=1.25 EndY=-20.6237 EndZ=0
    g28: LineSegment StartX=4.3229 StartY=-15.75 StartZ=0 EndX=6.12372 EndY=-15.75 EndZ=0
    g29: LineSegment StartX=4.3229 StartY=-13.25 StartZ=0 EndX=6.12372 EndY=-13.25 EndZ=0
    g30: LineSegment StartX=1.25 StartY=-10.1771 StartZ=0 EndX=1.25 EndY=-8.37628 EndZ=0
    g31: LineSegment StartX=-1.25 StartY=-8.37628 StartZ=0 EndX=-1.25 EndY=-10.1771 EndZ=0
  constraints (95):
    c: Coincident(g8,g6)
    c: Coincident(g8,g7)
    c: Coincident(g9,g0)
    c: Coincident(g9,g1)
    c: Coincident(g10,g1)
    c: Coincident(g10,g0)
    c: Coincident(g11,g3)
    c: Coincident(g11,g2)
    c: Coincident(g12,g3)
    c: Coincident(g12,g2)
    c: Coincident(g13,g4)
    c: Coincident(g13,g5)
    c: Coincident(g14,g4)
    c: Coincident(g14,g5)
    c: Coincident(g15,g7)
    c: Coincident(g15,g6)
    c: Coincident(g4,g2)
    c: Coincident(g4,g3)
    c: Coincident(g4,g1)
    c: Coincident(g4,g0)
    c: Coincident(g4,g7)
    c: Coincident(g4,g6)
    c: Coincident(g4,g-3)
    c: Vertical(g10)
    c: Vertical(g11)
    c: Vertical(g15)
    c: Vertical(g14)
    c: Horizontal(g8)
    c: Horizontal(g13)
    c: Horizontal(g12)
    c: Horizontal(g9)
    c: Equal(g2,g5)
    c: Equal(g5,g7)
    c: Equal(g6,g4)
    c: Equal(g4,g3)
    c: Equal(g3,g1)
    c: Coincident(g5,g0)
    c: Symmetric(g0,g2,g-2)
    c: Vertical(g1,g6)
    c: Equal(g10,g9)
    c: Equal(g9,g8)
    c: Equal(g15,g14)
    c: Equal(g14,g13)
    c: Equal(g13,g12)
    c: DistanceX(g0,g2) = 2.5  'WallThickness'
    c: Diameter(g4) = 9
    c: Diameter(g5) = 12.5
    c: Coincident(g24,g22)
    c: Coincident(g24,g23)
    c: Coincident(g25,g16)
    c: Coincident(g25,g17)
    c: Coincident(g26,g17)
    c: Coincident(g26,g16)
    c: Coincident(g27,g19)
    c: Coincident(g27,g18)
    c: Coincident(g28,g19)
    c: Coincident(g28,g18)
    c: Coincident(g29,g20)
    c: Coincident(g29,g21)
    c: Coincident(g30,g20)
    c: Coincident(g30,g21)
    c: Coincident(g31,g23)
    c: Coincident(g31,g22)
    c: Coincident(g20,g18)
    c: Coincident(g20,g19)
    c: Coincident(g20,g17)
    c: Coincident(g20,g16)
    c: Coincident(g20,g23)
    c: Coincident(g20,g22)
    c: Vertical(g26)
    c: Vertical(g27)
    c: Vertical(g31)
    c: Vertical(g30)
    c: Horizontal(g24)
    c: Horizontal(g29)
    c: Horizontal(g28)
    c: Horizontal(g25)
    c: Equal(g18,g21)
    c: Equal(g21,g23)
    c: Equal(g22,g20)
    c: Equal(g20,g19)
    c: Equal(g19,g17)
    c: Coincident(g21,g16)
    c: Equal(g26,g25)
    c: Equal(g25,g24)
    c: Equal(g31,g30)
    c: Equal(g30,g29)
    c: Equal(g29,g28)
    c: Diameter(g20) = 9
    c: Diameter(g21) = 12.5
    c: Coincident(g16,g-4)
    c: Vertical(g5,g21)
    c: Vertical(g21,g19)
    c: Vertical(g22,g17)
    c: Horizontal(g22,g20)
FEATURE [PartDesign::Pocket] Pocket017
  BaseFeature = -> Pad008
  Direction = (0,0,-1)
  Length = 5
  Length2 = 5
  Profile = -> Sketch032
  ReferenceAxis = -> Sketch032 [N_Axis]
  Refine = true
  Suppressed = false
  Type = 1
FEATURE [Sketcher::SketchObject] Sketch033
  ArcFitTolerance = 1e-06
  AttachmentSupport = -> [Pocket017]
  ExternalGeometry = -> [Pocket017]
  ExternalTypes = [0]
  FullyConstrained = true
  MakeInternals = false
  MapMode = 5
  Placement = pos=(0,0,35) rot=(0,0,1;0rad)
  expr: Constraints[10] = <<Sketch032>>.Constraints.WallThickness
  expr: Constraints[11] = <<Sketch032>>.Constraints.WallThickness
  sketch-geometry (5):
    g0: LineSegment StartX=-5.5 StartY=-0.5 StartZ=0 EndX=-5.5 EndY=0.5 EndZ=0
    g1: LineSegment StartX=-5.5 StartY=0.5 StartZ=0 EndX=5.5 EndY=0.5 EndZ=0
    g2: LineSegment StartX=5.5 StartY=0.5 StartZ=0 EndX=5.5 EndY=-0.5 EndZ=0
    g3: LineSegment StartX=5.5 StartY=-0.5 StartZ=0 EndX=-5.5 EndY=-0.5 EndZ=0
    g4: GeomPoint [constr] X=0 Y=0 Z=0
  constraints (12):
    c: Coincident(g0,g1)
    c: Coincident(g1,g2)
    c: Coincident(g2,g3)
    c: Coincident(g3,g0)
    c: Vertical(g0)
    c: Vertical(g2)
    c: Horizontal(g1)
    c: Horizontal(g3)
    c: Symmetric(g2,g0,g4)
    c: Coincident(g4,g-1)
    c: DistanceY(g0,g-3) = 2.5
    c: DistanceX(g-3,g0) = 2.5
FEATURE [PartDesign::Pocket] Pocket018
  BaseFeature = -> Pocket017
  Direction = (0,0,-1)
  Length = 10
  Length2 = 5
  Profile = -> Sketch033
  ReferenceAxis = -> Sketch033 [N_Axis]
  Refine = true
  Suppressed = false
  Type = 0
FEATURE [Sketcher::SketchObject] Sketch034
  ArcFitTolerance = 1e-06
  AttachmentSupport = -> [Pocket018]
  ExternalGeometry = -> [Pocket018]
  ExternalTypes = [0]
  FullyConstrained = true
  MakeInternals = false
  MapMode = 5
  Placement = pos=(0,0,0) rot=(1,0,0;3.14159rad)
  expr: Constraints[10] = <<Sketch032>>.Constraints.WallThickness
  expr: Constraints[11] = <<Sketch032>>.Constraints.WallThickness
  sketch-geometry (5):
    g0: LineSegment StartX=-5.5 StartY=-0.5 StartZ=0 EndX=-5.5 EndY=0.5 EndZ=0
    g1: LineSegment StartX=-5.5 StartY=0.5 StartZ=0 EndX=5.5 EndY=0.5 EndZ=0
    g2: LineSegment StartX=5.5 StartY=0.5 StartZ=0 EndX=5.5 EndY=-0.5 EndZ=0
    g3: LineSegment StartX=5.5 StartY=-0.5 StartZ=0 EndX=-5.5 EndY=-0.5 EndZ=0
    g4: GeomPoint [constr] X=0 Y=0 Z=0
  constraints (12):
    c: Coincident(g0,g1)
    c: Coincident(g1,g2)
    c: Coincident(g2,g3)
    c: Coincident(g3,g0)
    c: Vertical(g0)
    c: Vertical(g2)
    c: Horizontal(g1)
    c: Horizontal(g3)
    c: Symmetric(g2,g0,g4)
    c: Coincident(g4,g-1)
    c: DistanceY(g0,g-3) = 2.5
    c: DistanceX(g-3,g0) = 2.5
FEATURE [PartDesign::Pocket] Pocket019
  BaseFeature = -> Pocket018
  Direction = (0,0,1)
  Length = 0
  Length2 = 5
  Offset = 10
  Profile = -> Sketch034
  ReferenceAxis = -> Sketch034 [N_Axis]
  Refine = true
  Suppressed = false
  Type = 3
  UpToFace = -> Pocket018 [Face69]
FEATURE [Sketcher::SketchObject] Sketch035
  ArcFitTolerance = 1e-06
  AttachmentSupport = -> [Pocket019]
  ExternalTypes = [0]
  FullyConstrained = true
  MakeInternals = false
  MapMode = 5
  Placement = pos=(0,0,35) rot=(0,0,1;0rad)
  sketch-geometry (1):
    g0: Circle CenterX=0 CenterY=0 CenterZ=0 NormalX=0 NormalY=0 NormalZ=1 AngleXU=0 Radius=6
  constraints (2):
    c: Coincident(g0,g-1)
    c: Diameter(g0) = 12
FEATURE [PartDesign::Pocket] Pocket020
  BaseFeature = -> Pocket019
  Direction = (0,0,-1)
  Length = 0
  Length2 = 5
  Profile = -> Sketch035
  ReferenceAxis = -> Sketch035 [N_Axis]
  Refine = true
  Suppressed = false
  Type = 3
  UpToFace = -> Pocket019 [Face77]
FEATURE [PartDesign::Chamfer] Chamfer003
  Angle = 45
  Base = -> Pocket020 [Edge188,Edge186,Vertex132]
  BaseFeature = -> Pocket020
  ChamferType = 0
  FlipDirection = false
  Refine = true
  Size = 2.9
  Size2 = 1
  SupportTransform = false
  Suppressed = false
  UseAllEdges = false
FEATURE [PartDesign::Body] Body004  label="Dual Pipes 29mm"
  AllowCompound = false
  Group = -> [Sketch029,Pad007,Sketch030,Pocket016,Sketch031,Pad008,Sketch032,Pocket017,Sketch033,Pocket018,Sketch034,Pocket019,Sketch035,Pocket020,Chamfer003]
  Origin = -> Origin012
  Tip = -> Chamfer003
PROVENANCE & LICENSES
A FreeCAD (.FCStd) document from a public repository crawl; recipes are the document's own serialized feature recipes (and, for linked parts, companion documents' recipes).
License: as declared in the source repository (recorded in the dataset sidecar).
